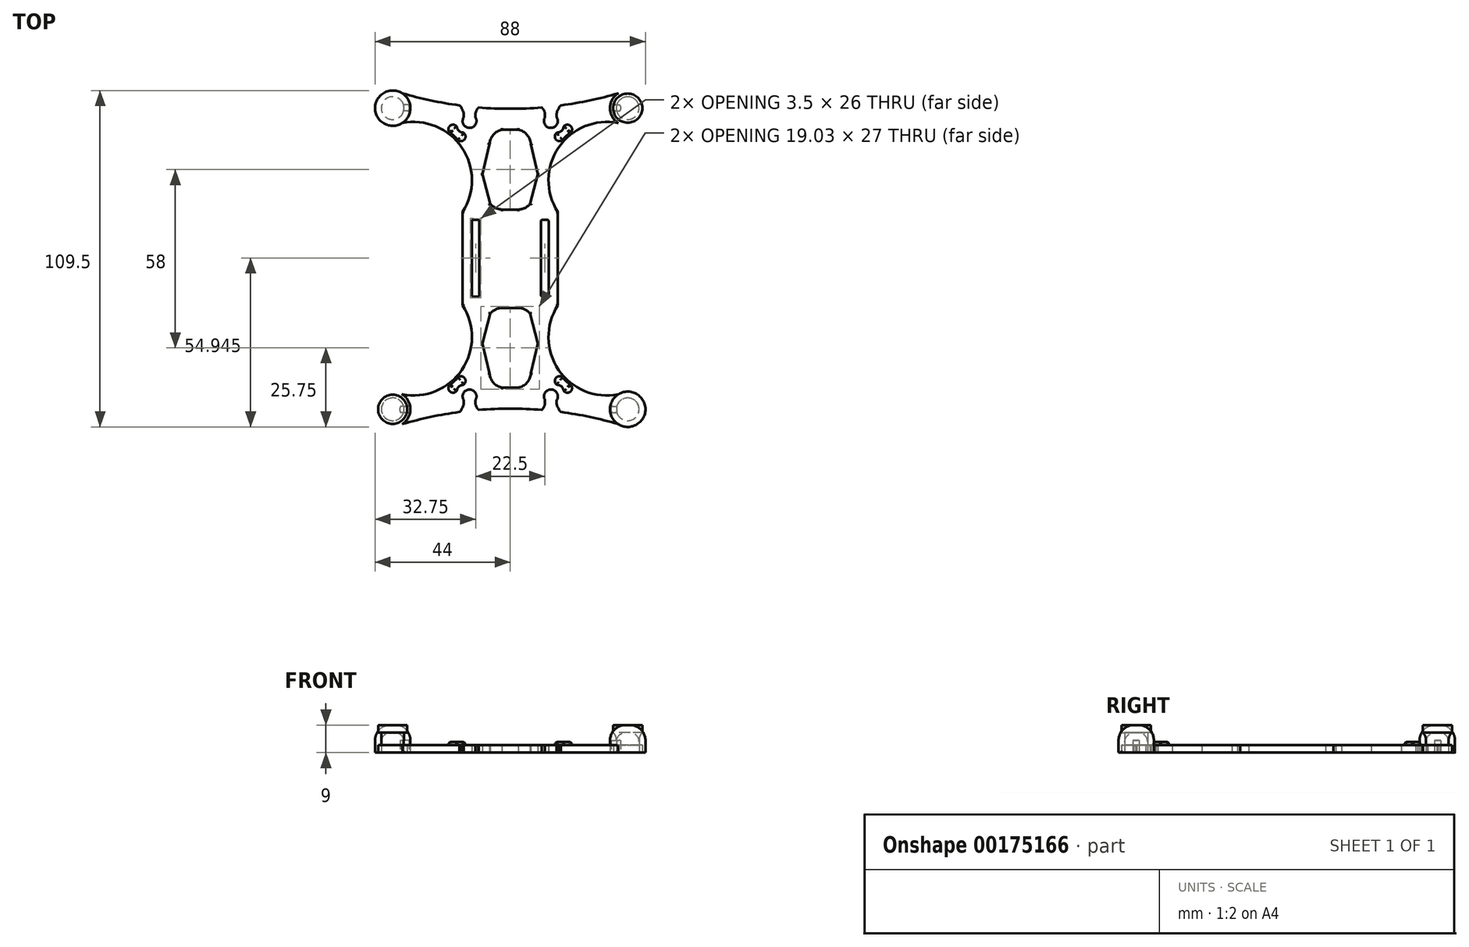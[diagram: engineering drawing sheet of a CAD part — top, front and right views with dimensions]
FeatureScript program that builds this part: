
annotation { "Feature Type Name" : "Feature", "Feature Type Description" : "" }
export const myFeature = defineFeature(function(context is Context, id is Id, definition is map)
    precondition{}
    {
        {
            assignVariable(context, id + "F0", {"name" : "FrameHeight", "anyValue" : 2.5});
        }
        {
            var Q0;
            Q0=qCreatedBy(makeId("Top.planeOp"),FACE);
            var sketch = newSketch(context, id + "F1", { "sketchPlane" : qUnion([Q0])});
            skPoint(sketch, "E0.middle", {"position": v(0, 0) * mm});
            skCircle(sketch, "E1", {"center": v(-38.25, 49) * mm, "radius": 5.75 * mm});
            skCircle(sketch, "E2.MirrorC", {"center": v(38.25, 49) * mm, "radius": 5.75 * mm});
            skCircle(sketch, "E3.MirrorC", {"center": v(-38.25, -49) * mm, "radius": 5.75 * mm});
            skCircle(sketch, "E4.MirrorC", {"center": v(38.25, -49) * mm, "radius": 5.75 * mm});
            skArc(sketch, "E5", {"start": v(-35.12, 53.82) * mm, "mid": v(-25.9, 51.5) * mm, "end": v(-16.55, 49.89) * mm});
            skCircle(sketch, "E6", {"center": v(-38.25, 49) * mm, "radius": 3.7 * mm});
            skCircle(sketch, "E7.MirrorC", {"center": v(38.25, 49) * mm, "radius": 3.7 * mm});
            skCircle(sketch, "E8.MirrorC", {"center": v(38.25, -49) * mm, "radius": 3.7 * mm});
            skCircle(sketch, "E9.MirrorC", {"center": v(-38.25, -49) * mm, "radius": 3.7 * mm});
            skPoint(sketch, "E10.MirrorP", {"position": v(-9, -27.55) * mm});
            skArc(sketch, "E11.MirrorCS", {"start": v(-2.66, -42) * mm, "mid": v(-5.49, -40.33) * mm, "end": v(-6.7, -37.29) * mm});
            skArc(sketch, "E12.MirrorCS", {"start": v(-2.66, -16) * mm, "mid": v(-4.79, -16.51) * mm, "end": v(-6.5, -17.87) * mm});
            skLineSegment(sketch, "E13", {"start": v(-6.5, -17.87) * mm, "end": v(-9, -27.55) * mm});
            skLineSegment(sketch, "E14", {"start": v(-6.7, -37.29) * mm, "end": v(-9, -27.55) * mm});
            skArc(sketch, "E15.MirrorCS", {"start": v(2.66, -16) * mm, "mid": v(4.79, -16.51) * mm, "end": v(6.5, -17.87) * mm});
            skLineSegment(sketch, "E16.MirrorCS", {"start": v(6.5, -17.87) * mm, "end": v(9, -27.55) * mm});
            skLineSegment(sketch, "E17.MirrorCS", {"start": v(6.7, -37.29) * mm, "end": v(9, -27.55) * mm});
            skArc(sketch, "E18.MirrorCS", {"start": v(2.66, -42) * mm, "mid": v(5.49, -40.33) * mm, "end": v(6.7, -37.29) * mm});
            skLineSegment(sketch, "E19", {"start": v(-2.66, -16) * mm, "end": v(2.66, -16) * mm});
            skLineSegment(sketch, "E20", {"start": v(2.66, -42) * mm, "end": v(-2.66, -42) * mm});
            skLineSegment(sketch, "E21.MirrorCS", {"start": v(-2.66, 16) * mm, "end": v(2.66, 16) * mm});
            skArc(sketch, "E22.MirrorCS", {"start": v(-2.66, 16) * mm, "mid": v(-4.79, 16.51) * mm, "end": v(-6.5, 17.87) * mm});
            skLineSegment(sketch, "E23.MirrorCS", {"start": v(-6.5, 17.87) * mm, "end": v(-9, 27.55) * mm});
            skArc(sketch, "E24.MirrorCS", {"start": v(2.66, 16) * mm, "mid": v(4.79, 16.51) * mm, "end": v(6.5, 17.87) * mm});
            skLineSegment(sketch, "E25.MirrorCS", {"start": v(6.5, 17.87) * mm, "end": v(9, 27.55) * mm});
            skLineSegment(sketch, "E26.MirrorCS", {"start": v(-6.7, 37.29) * mm, "end": v(-9, 27.55) * mm});
            skLineSegment(sketch, "E27.MirrorCS", {"start": v(6.7, 37.29) * mm, "end": v(9, 27.55) * mm});
            skArc(sketch, "E28.MirrorCS", {"start": v(2.66, 42) * mm, "mid": v(5.49, 40.33) * mm, "end": v(6.7, 37.29) * mm});
            skLineSegment(sketch, "E29.MirrorCS", {"start": v(2.66, 42) * mm, "end": v(-2.66, 42) * mm});
            skArc(sketch, "E30.MirrorCS", {"start": v(-2.66, 42) * mm, "mid": v(-5.49, 40.33) * mm, "end": v(-6.7, 37.29) * mm});
            skArc(sketch, "E31", {"start": v(-15.5, 15.2) * mm, "mid": v(-15.74, 36.19) * mm, "end": v(-35.17, 44.14) * mm});
            skArc(sketch, "E32.MirrorCS", {"start": v(-35.12, -53.82) * mm, "mid": v(-25.9, -51.5) * mm, "end": v(-16.55, -49.89) * mm});
            skArc(sketch, "E33.MirrorCS", {"start": v(15.5, 15.2) * mm, "mid": v(15.74, 36.19) * mm, "end": v(35.17, 44.14) * mm});
            skArc(sketch, "E34.MirrorCS", {"start": v(15.5, -15.2) * mm, "mid": v(15.74, -36.19) * mm, "end": v(35.17, -44.14) * mm});
            skArc(sketch, "E35.MirrorCS", {"start": v(-15.5, -15.2) * mm, "mid": v(-15.74, -36.19) * mm, "end": v(-35.17, -44.14) * mm});
            skLineSegment(sketch, "E36", {"start": v(-15.5, -15.2) * mm, "end": v(-15.5, 15.2) * mm});
            skLineSegment(sketch, "E37.bottom", {"start": v(-12, -12.3) * mm, "end": v(-10.5, -12.3) * mm});
            skLineSegment(sketch, "E37.top", {"start": v(-12, 12.7) * mm, "end": v(-10.5, 12.7) * mm});
            skLineSegment(sketch, "E37.left", {"start": v(-12.5, -11.8) * mm, "end": v(-12.5, 12.2) * mm});
            skLineSegment(sketch, "E37.right", {"start": v(-10, -11.8) * mm, "end": v(-10, 12.2) * mm});
            skLineSegment(sketch, "E38", {"start": v(-15.5, 15.2) * mm, "end": v(15.5, 15.2) * mm, "construction": true});
            skPoint(sketch, "E39.visualSharp", {"position": v(-10, -12.3) * mm});
            skArc(sketch, "E39.filletArc", {"start": v(-10.5, -12.3) * mm, "mid": v(-10.15, -12.16) * mm, "end": v(-10, -11.8) * mm});
            skPoint(sketch, "E40.visualSharp", {"position": v(-12.5, -12.3) * mm});
            skArc(sketch, "E40.filletArc", {"start": v(-12.5, -11.8) * mm, "mid": v(-12.35, -12.16) * mm, "end": v(-12, -12.3) * mm});
            skPoint(sketch, "E41.visualSharp", {"position": v(-10, 12.7) * mm});
            skArc(sketch, "E41.filletArc", {"start": v(-10, 12.2) * mm, "mid": v(-10.15, 12.55) * mm, "end": v(-10.5, 12.7) * mm});
            skPoint(sketch, "E42.visualSharp", {"position": v(-12.5, 12.7) * mm});
            skArc(sketch, "E42.filletArc", {"start": v(-12, 12.7) * mm, "mid": v(-12.35, 12.55) * mm, "end": v(-12.5, 12.2) * mm});
            skLineSegment(sketch, "E43.MirrorCS", {"start": v(12, -12.3) * mm, "end": v(10.5, -12.3) * mm});
            skArc(sketch, "E44.MirrorCS", {"start": v(12.5, -11.8) * mm, "mid": v(12.35, -12.16) * mm, "end": v(12, -12.3) * mm});
            skArc(sketch, "E45.MirrorCS", {"start": v(10.5, -12.3) * mm, "mid": v(10.15, -12.16) * mm, "end": v(10, -11.8) * mm});
            skLineSegment(sketch, "E46.MirrorCS", {"start": v(10, -11.8) * mm, "end": v(10, 12.2) * mm});
            skLineSegment(sketch, "E47.MirrorCS", {"start": v(12.5, -11.8) * mm, "end": v(12.5, 12.2) * mm});
            skArc(sketch, "E48.MirrorCS", {"start": v(10, 12.2) * mm, "mid": v(10.15, 12.55) * mm, "end": v(10.5, 12.7) * mm});
            skLineSegment(sketch, "E49.MirrorCS", {"start": v(12, 12.7) * mm, "end": v(10.5, 12.7) * mm});
            skArc(sketch, "E50.MirrorCS", {"start": v(12, 12.7) * mm, "mid": v(12.35, 12.55) * mm, "end": v(12.5, 12.2) * mm});
            skLineSegment(sketch, "E51", {"start": v(15.5, 15.2) * mm, "end": v(15.5, -15.2) * mm});
            skArc(sketch, "E52.trimOffspring", {"start": v(-10.28, 49.21) * mm, "mid": v(0, 48.79) * mm, "end": v(10.28, 49.21) * mm});
            skArc(sketch, "E53", {"start": v(-15.18, 45.95) * mm, "mid": v(-13.3, 42.57) * mm, "end": v(-11.24, 45.85) * mm});
            skArc(sketch, "E54", {"start": v(-15.18, 45.95) * mm, "mid": v(-15.18, 47.49) * mm, "end": v(-15.83, 48.88) * mm});
            skArc(sketch, "E55.MirrorCS", {"start": v(-11.24, 45.85) * mm, "mid": v(-11.2, 47.66) * mm, "end": v(-10.28, 49.21) * mm});
            skArc(sketch, "E56.trimOffspring", {"start": v(16.55, 49.89) * mm, "mid": v(25.9, 51.5) * mm, "end": v(35.12, 53.82) * mm});
            skArc(sketch, "E57.trimOffspring", {"start": v(-10.28, -49.21) * mm, "mid": v(0, -48.79) * mm, "end": v(10.28, -49.21) * mm});
            skArc(sketch, "E58.trimOffspring", {"start": v(16.55, -49.89) * mm, "mid": v(25.9, -51.5) * mm, "end": v(35.12, -53.82) * mm});
            skArc(sketch, "E59.MirrorCS", {"start": v(11.24, 45.85) * mm, "mid": v(11.2, 47.66) * mm, "end": v(10.28, 49.21) * mm});
            skArc(sketch, "E60.MirrorCS", {"start": v(15.18, 45.95) * mm, "mid": v(15.18, 47.49) * mm, "end": v(15.83, 48.88) * mm});
            skArc(sketch, "E61.MirrorCS", {"start": v(15.18, 45.95) * mm, "mid": v(13.3, 42.57) * mm, "end": v(11.24, 45.85) * mm});
            skArc(sketch, "E62.MirrorCS", {"start": v(15.18, -45.95) * mm, "mid": v(13.3, -42.57) * mm, "end": v(11.24, -45.85) * mm});
            skArc(sketch, "E63.MirrorCS", {"start": v(11.24, -45.85) * mm, "mid": v(11.2, -47.66) * mm, "end": v(10.28, -49.21) * mm});
            skArc(sketch, "E64.MirrorCS", {"start": v(15.18, -45.95) * mm, "mid": v(15.18, -47.49) * mm, "end": v(15.83, -48.88) * mm});
            skArc(sketch, "E65.MirrorCS", {"start": v(-11.24, -45.85) * mm, "mid": v(-11.2, -47.66) * mm, "end": v(-10.28, -49.21) * mm});
            skArc(sketch, "E66.MirrorCS", {"start": v(-15.18, -45.95) * mm, "mid": v(-15.18, -47.49) * mm, "end": v(-15.83, -48.88) * mm});
            skArc(sketch, "E67.MirrorCS", {"start": v(-15.18, -45.95) * mm, "mid": v(-13.3, -42.57) * mm, "end": v(-11.24, -45.85) * mm});
            skLineSegment(sketch, "E68", {"start": v(-38.25, 49) * mm, "end": v(38.25, 49) * mm, "construction": true});
            skArc(sketch, "E69", {"start": v(16.55, 49.89) * mm, "mid": v(16.05, 49.49) * mm, "end": v(15.83, 48.88) * mm});
            skArc(sketch, "E70.MirrorCS", {"start": v(-16.55, 49.89) * mm, "mid": v(-16.05, 49.49) * mm, "end": v(-15.83, 48.88) * mm});
            skArc(sketch, "E71.MirrorCS", {"start": v(-16.55, -49.89) * mm, "mid": v(-16.05, -49.49) * mm, "end": v(-15.83, -48.88) * mm});
            skArc(sketch, "E72.MirrorCS", {"start": v(16.55, -49.89) * mm, "mid": v(16.05, -49.49) * mm, "end": v(15.83, -48.88) * mm});
            skLineSegment(sketch, "E73", {"start": v(-38.25, -49) * mm, "end": v(38.25, 49) * mm, "construction": true});
            skCircle(sketch, "E74", {"center": v(-38.25, 49) * mm, "radius": 4.75 * mm});
            skCircle(sketch, "E75.MirrorC", {"center": v(38.25, 49) * mm, "radius": 4.75 * mm});
            skCircle(sketch, "E76.MirrorC", {"center": v(38.25, -49) * mm, "radius": 4.75 * mm});
            skCircle(sketch, "E77.MirrorC", {"center": v(-38.25, -49) * mm, "radius": 4.75 * mm});
            skSolve(sketch);
        }
        {
            var Q0;
            {var subQ4=sQuery(id+"F1.wireOp",EDGE,"E5");Q0=makeQuery(id+"F1.imprint","IMPRINT",FACE,{"disambiguationData":[TD([[makeQuery(id+"F1.imprint","IMPRINT",EDGE,{"derivedFrom":subQ4}),-1.0]])]});}
            var Q1;
            Q1=makeQuery(id+"F1.imprint","IMPRINT",FACE,{"disambiguationData":[TD([[makeQuery(id+"F1.imprint","IMPRINT",EDGE,{"derivedFrom":sQuery(id+"F1.wireOp",EDGE,"E9.MirrorC")}),1.0]])]});
            var Q2;
            Q2=makeQuery(id+"F1.imprint","IMPRINT",FACE,{"disambiguationData":[TD([[makeQuery(id+"F1.imprint","IMPRINT",EDGE,{"derivedFrom":sQuery(id+"F1.wireOp",EDGE,"E8.MirrorC")}),-1.0]])]});
            var Q3;
            Q3=makeQuery(id+"F1.imprint","IMPRINT",FACE,{"disambiguationData":[TD([[makeQuery(id+"F1.imprint","IMPRINT",EDGE,{"derivedFrom":sQuery(id+"F1.wireOp",EDGE,"E6")}),-1.0]])]});
            var Q4;
            Q4=makeQuery(id+"F1.imprint","IMPRINT",FACE,{"disambiguationData":[TD([[makeQuery(id+"F1.imprint","IMPRINT",EDGE,{"derivedFrom":sQuery(id+"F1.wireOp",EDGE,"E7.MirrorC")}),1.0]])]});
            var Q5;
            {var subQ0=sQuery(id+"F1.wireOp",EDGE,"7a08c846-7200-404a-ab22-a396ae0e95b40.MirrorCS");Q5=makeQuery(id+"F1.imprint","IMPRINT",FACE,{"disambiguationData":[TD([[makeQuery(id+"F1.imprint","IMPRINT",EDGE,{"derivedFrom":subQ0}),-1.0]])]});}
            extrude(context, id + "F2", {"entities" : qUnion([Q0, Q1, Q2, Q3, Q4, Q5]), "depth" : 2.5 * mm});
        }
        {
            var Q0;
            Q0=makeQuery(id+"F1.imprint","IMPRINT",FACE,{"disambiguationData":[TD([[makeQuery(id+"F1.imprint","IMPRINT",EDGE,{"derivedFrom":sQuery(id+"F1.wireOp",EDGE,"E74")}),-1.0]])]});
            var Q1;
            Q1=makeQuery(id+"F1.imprint","IMPRINT",FACE,{"disambiguationData":[TD([[makeQuery(id+"F1.imprint","IMPRINT",EDGE,{"derivedFrom":sQuery(id+"F1.wireOp",EDGE,"E75.MirrorC")}),1.0]])]});
            var Q2;
            Q2=makeQuery(id+"F1.imprint","IMPRINT",FACE,{"disambiguationData":[TD([[makeQuery(id+"F1.imprint","IMPRINT",EDGE,{"derivedFrom":sQuery(id+"F1.wireOp",EDGE,"E77.MirrorC")}),1.0]])]});
            var Q3;
            Q3=makeQuery(id+"F1.imprint","IMPRINT",FACE,{"disambiguationData":[TD([[makeQuery(id+"F1.imprint","IMPRINT",EDGE,{"derivedFrom":sQuery(id+"F1.wireOp",EDGE,"E76.MirrorC")}),-1.0]])]});
            extrude(context, id + "F3", {"entities" : qUnion([Q0, Q1, Q2, Q3]), "operationType" : NewBodyOperationType.ADD, "depth" : 3 * mm});
        }
        {
            var Q0;
            Q0=makeQuery(id+"F1.imprint","IMPRINT",FACE,{"disambiguationData":[TD([[makeQuery(id+"F1.imprint","IMPRINT",EDGE,{"derivedFrom":sQuery(id+"F1.wireOp",EDGE,"E6")}),-1.0]])]});
            var Q1;
            Q1=makeQuery(id+"F1.imprint","IMPRINT",FACE,{"disambiguationData":[TD([[makeQuery(id+"F1.imprint","IMPRINT",EDGE,{"derivedFrom":sQuery(id+"F1.wireOp",EDGE,"E7.MirrorC")}),1.0]])]});
            var Q2;
            Q2=makeQuery(id+"F1.imprint","IMPRINT",FACE,{"disambiguationData":[TD([[makeQuery(id+"F1.imprint","IMPRINT",EDGE,{"derivedFrom":sQuery(id+"F1.wireOp",EDGE,"E9.MirrorC")}),1.0]])]});
            var Q3;
            Q3=makeQuery(id+"F1.imprint","IMPRINT",FACE,{"disambiguationData":[TD([[makeQuery(id+"F1.imprint","IMPRINT",EDGE,{"derivedFrom":sQuery(id+"F1.wireOp",EDGE,"E8.MirrorC")}),-1.0]])]});
            var Q4;
            Q4=makeQuery(id+"F1.imprint","IMPRINT",FACE,{"disambiguationData":[TD([[makeQuery(id+"F1.imprint","IMPRINT",EDGE,{"derivedFrom":sQuery(id+"F1.wireOp",EDGE,"E6")}),1.0]])]});
            var Q5;
            Q5=makeQuery(id+"F1.imprint","IMPRINT",FACE,{"disambiguationData":[TD([[makeQuery(id+"F1.imprint","IMPRINT",EDGE,{"derivedFrom":sQuery(id+"F1.wireOp",EDGE,"E7.MirrorC")}),-1.0]])]});
            var Q6;
            Q6=makeQuery(id+"F1.imprint","IMPRINT",FACE,{"disambiguationData":[TD([[makeQuery(id+"F1.imprint","IMPRINT",EDGE,{"derivedFrom":sQuery(id+"F1.wireOp",EDGE,"E8.MirrorC")}),1.0]])]});
            var Q7;
            Q7=makeQuery(id+"F1.imprint","IMPRINT",FACE,{"disambiguationData":[TD([[makeQuery(id+"F1.imprint","IMPRINT",EDGE,{"derivedFrom":sQuery(id+"F1.wireOp",EDGE,"E9.MirrorC")}),-1.0]])]});
            var Q8;
            {var subQ0=sQuery(id+"F1.wireOp",EDGE,"ea4f1012-2509-42ab-b6be-2330c5534f0a0.MirrorCS");var subQ1=sQuery(id+"F1.wireOp",EDGE,"cdfdab9b-bf2e-43ec-8392-f97786d2ea0d0.MirrorCS");var subQ2=sQuery(id+"F1.wireOp",EDGE,"465e94d3-5aed-43b1-ab28-4905a897ac150.MirrorCS");var subQ3=sQuery(id+"F1.wireOp",EDGE,"98a759bb-2186-4722-986c-5ad8236f98b60.MirrorCS");var subQ4=sQuery(id+"F1.wireOp",EDGE,"529e4913-d2e2-4b9c-8764-fd74a515156b0.MirrorCS");var subQ5=sQuery(id+"F1.wireOp",EDGE,"a75351e4-8b9f-4b28-a4a3-4962784478ad0.MirrorCS");var subQ6=sQuery(id+"F1.wireOp",EDGE,"82538637-7302-4e28-b2d0-c30d791653240.MirrorCS");var subQ7=sQuery(id+"F1.wireOp",EDGE,"56e68159-8ace-49cd-9e0b-4dd6a05a3e180.MirrorCS");var subQ8=sQuery(id+"F1.wireOp",EDGE,"e7e79bb3-8a2c-4938-af19-8f637f7eba370.MirrorCS");var subQ9=sQuery(id+"F1.wireOp",EDGE,"2316bcf3-3be9-4e9e-b8e2-497a6a1952b90.MirrorCS");var subQ10=sQuery(id+"F1.wireOp",EDGE,"1773aba8-4819-4f46-a8a7-8d94881a3e2a0.MirrorCS");var subQ11=sQuery(id+"F1.wireOp",EDGE,"e0e34dce-b0e1-4d64-a790-8c4829cf73b10.MirrorCS");var subQ12=sQuery(id+"F1.wireOp",EDGE,"8cd6d0e1-198d-4ddf-9674-687771b3d4800.MirrorCS");var subQ13=sQuery(id+"F1.wireOp",EDGE,"258af2fb-57e0-4cd8-8c30-8cafca4a9de30.MirrorCS");var subQ14=sQuery(id+"F1.wireOp",EDGE,"a07b8381-fd63-4e58-856e-6aaff1297d55.filletArc");var subQ15=sQuery(id+"F1.wireOp",EDGE,"RvagwD08-4saL-jRzY-J36Z-niyVwtinKrBz");var subQ16=sQuery(id+"F1.wireOp",EDGE,"o4VfrY1E-f77m-jJ6D-3hSz-oWbsnZmPJ7RM");var subQ17=sQuery(id+"F1.wireOp",EDGE,"5SzH9PIc-MBC3-JWxo-jWJ1-gy0vg8dHxIne");var subQ18=sQuery(id+"F1.wireOp",EDGE,"Skl9KyDn-OFwj-jcuM-sPno-qYqNKXC7fZA3");var subQ19=sQuery(id+"F1.wireOp",EDGE,"5RGUndvU-jcMW-WSWi-Bxv8-2VV6o0UGLXlU");var subQ20=sQuery(id+"F1.wireOp",EDGE,"NKQneA6F-sO9O-ycv6-QC4M-7Sw9j2aKeUUz");var subQ21=sQuery(id+"F1.wireOp",EDGE,"41db651c-dc80-447a-ac2a-c1855a6981c0.filletArc");var subQ22=sQuery(id+"F1.wireOp",EDGE,"cd34b8fd-3b9d-40b5-866b-1931df3bf95f.filletArc");var subQ23=sQuery(id+"F1.wireOp",EDGE,"e2ad8a51-9023-4a85-890f-8adf256902f4.filletArc");var subQ24=sQuery(id+"F1.wireOp",EDGE,"f659aba6-3ceb-4f67-afd8-6bc25f8b2d52.filletArc");var subQ25=sQuery(id+"F1.wireOp",EDGE,"E30.MirrorCS");var subQ26=sQuery(id+"F1.wireOp",EDGE,"E29.MirrorCS");var subQ27=sQuery(id+"F1.wireOp",EDGE,"E28.MirrorCS");var subQ28=sQuery(id+"F1.wireOp",EDGE,"E27.MirrorCS");var subQ29=sQuery(id+"F1.wireOp",EDGE,"E26.MirrorCS");var subQ30=sQuery(id+"F1.wireOp",EDGE,"E25.MirrorCS");var subQ31=sQuery(id+"F1.wireOp",EDGE,"E24.MirrorCS");var subQ32=sQuery(id+"F1.wireOp",EDGE,"E23.MirrorCS");var subQ33=sQuery(id+"F1.wireOp",EDGE,"E22.MirrorCS");var subQ34=sQuery(id+"F1.wireOp",EDGE,"E21.MirrorCS");var subQ35=sQuery(id+"F1.wireOp",EDGE,"E20");var subQ36=sQuery(id+"F1.wireOp",EDGE,"E19");var subQ37=sQuery(id+"F1.wireOp",EDGE,"E18.MirrorCS");var subQ38=sQuery(id+"F1.wireOp",EDGE,"E17.MirrorCS");var subQ39=sQuery(id+"F1.wireOp",EDGE,"E16.MirrorCS");var subQ40=sQuery(id+"F1.wireOp",EDGE,"E15.MirrorCS");var subQ41=sQuery(id+"F1.wireOp",EDGE,"E14");var subQ42=sQuery(id+"F1.wireOp",EDGE,"E13");var subQ43=sQuery(id+"F1.wireOp",EDGE,"E12.MirrorCS");var subQ44=sQuery(id+"F1.wireOp",EDGE,"E11.MirrorCS");var subQ45=sQuery(id+"F1.wireOp",EDGE,"8O0KtBdD-sCAZ-nUyN-ZE4b-Pr8atPqkOLOt.right");var subQ46=sQuery(id+"F1.wireOp",EDGE,"8O0KtBdD-sCAZ-nUyN-ZE4b-Pr8atPqkOLOt.top");var subQ47=sQuery(id+"F1.wireOp",EDGE,"8O0KtBdD-sCAZ-nUyN-ZE4b-Pr8atPqkOLOt.bottom");var subQ48=sQuery(id+"F1.wireOp",EDGE,"3a3e3443-e76c-4b3f-931a-bba0a9ca54bb0.MirrorC");var subQ49=sQuery(id+"F1.wireOp",EDGE,"5ae8c34d-aa19-45d0-b816-4b0481c35e6e0.MirrorC");var subQ50=sQuery(id+"F1.wireOp",EDGE,"e54bd452-817c-44b1-b4a1-4a82a5b737490.MirrorC");var subQ51=sQuery(id+"F1.wireOp",EDGE,"vB4YpJxw-nM1r-KAMU-Z2z7-AA1Xbjjr12VQ");var subQ52=sQuery(id+"F1.wireOp",EDGE,"2126723b-73e3-4daa-88ad-461916ae88fc0.MirrorCS");var subQ53=sQuery(id+"F1.wireOp",EDGE,"8d91ff8a-54ff-47bb-bb8d-6ed09a5a66a50.MirrorCS");var subQ54=sQuery(id+"F1.wireOp",EDGE,"462311f5-9079-46a5-b6e4-7ace82524d020.MirrorCS");var subQ55=sQuery(id+"F1.wireOp",EDGE,"8mwgoKQL-uejJ-Ytzu-yeJP-nfI78MkwDY2L");var subQ56=sQuery(id+"F1.wireOp",EDGE,"3589fe97-52ff-42bc-b7a9-5f631560aecf0.MirrorCS");var subQ57=sQuery(id+"F1.wireOp",EDGE,"E5");var subQ58=sQuery(id+"F1.wireOp",EDGE,"E4.MirrorC");var subQ59=sQuery(id+"F1.wireOp",EDGE,"E3.MirrorC");var subQ60=sQuery(id+"F1.wireOp",EDGE,"E2.MirrorC");var subQ61=sQuery(id+"F1.wireOp",EDGE,"E1");Q8=makeQuery(id+"FTKf5rjYO4gTYV3_1.boolean.opBoolean","MERGE",FACE,{"derivedFrom":[makeQuery(id+"FOrR15PyCScxact_0.opExtrude","CAP_FACE",FACE,{"disambiguationData":[OSD([subQ61,subQ60,subQ59,subQ58,subQ57,subQ56,subQ55,subQ54,subQ53,subQ52,subQ51,subQ50,subQ49,subQ48,subQ47,subQ46,subQ45,subQ44,subQ43,subQ42,subQ41,subQ40,subQ39,subQ38,subQ37,subQ36,subQ35,subQ34,subQ33,subQ32,subQ31,subQ30,subQ29,subQ28,subQ27,subQ26,subQ25,subQ24,subQ23,subQ22,subQ21,subQ20,subQ19,subQ18,subQ17,subQ16,subQ15,subQ14,subQ13,subQ12,subQ11,subQ10,subQ9,subQ8,subQ7,subQ6,subQ5,subQ4,subQ3,subQ2,subQ1,subQ0])],"isStart":false}),makeQuery(id+"FTKf5rjYO4gTYV3_1.opExtrude","CAP_FACE",FACE,{"disambiguationData":[OSD([subQ61,subQ60,subQ59,subQ58,subQ57,subQ56,sQuery(id+"F1.wireOp",EDGE,"E6"),subQ55,subQ54,subQ53,subQ52,sQuery(id+"F1.wireOp",EDGE,"E7.MirrorC"),sQuery(id+"F1.wireOp",EDGE,"E8.MirrorC"),sQuery(id+"F1.wireOp",EDGE,"E9.MirrorC"),subQ51,subQ50,subQ49,subQ48,subQ47,subQ46,subQ45,subQ44,subQ43,subQ42,subQ41,subQ40,subQ39,subQ38,subQ37,subQ36,subQ35,subQ34,subQ33,subQ32,subQ31,subQ30,subQ29,subQ28,subQ27,subQ26,subQ25,subQ24,subQ23,subQ22,subQ21,subQ20,subQ19,subQ18,subQ17,subQ16,subQ15,subQ14,subQ13,subQ12,subQ11,subQ10,subQ9,subQ8,subQ7,subQ6,subQ5,subQ4,subQ3,subQ2,subQ1,subQ0])],"isStart":false})]});}
            var Q9;
            Q9=makeQuery(id+"FOrR15PyCScxact_0.opExtrude","SWEPT_BODY",BODY,{"disambiguationData":[OSD([sQuery(id+"F1.wireOp",EDGE,"E1"),sQuery(id+"F1.wireOp",EDGE,"E2.MirrorC"),sQuery(id+"F1.wireOp",EDGE,"E3.MirrorC"),sQuery(id+"F1.wireOp",EDGE,"E4.MirrorC"),sQuery(id+"F1.wireOp",EDGE,"E5"),sQuery(id+"F1.wireOp",EDGE,"3589fe97-52ff-42bc-b7a9-5f631560aecf0.MirrorCS"),sQuery(id+"F1.wireOp",EDGE,"8mwgoKQL-uejJ-Ytzu-yeJP-nfI78MkwDY2L"),sQuery(id+"F1.wireOp",EDGE,"462311f5-9079-46a5-b6e4-7ace82524d020.MirrorCS"),sQuery(id+"F1.wireOp",EDGE,"8d91ff8a-54ff-47bb-bb8d-6ed09a5a66a50.MirrorCS"),sQuery(id+"F1.wireOp",EDGE,"2126723b-73e3-4daa-88ad-461916ae88fc0.MirrorCS"),sQuery(id+"F1.wireOp",EDGE,"vB4YpJxw-nM1r-KAMU-Z2z7-AA1Xbjjr12VQ"),sQuery(id+"F1.wireOp",EDGE,"e54bd452-817c-44b1-b4a1-4a82a5b737490.MirrorC"),sQuery(id+"F1.wireOp",EDGE,"5ae8c34d-aa19-45d0-b816-4b0481c35e6e0.MirrorC"),sQuery(id+"F1.wireOp",EDGE,"3a3e3443-e76c-4b3f-931a-bba0a9ca54bb0.MirrorC"),sQuery(id+"F1.wireOp",EDGE,"8O0KtBdD-sCAZ-nUyN-ZE4b-Pr8atPqkOLOt.bottom"),sQuery(id+"F1.wireOp",EDGE,"8O0KtBdD-sCAZ-nUyN-ZE4b-Pr8atPqkOLOt.top"),sQuery(id+"F1.wireOp",EDGE,"8O0KtBdD-sCAZ-nUyN-ZE4b-Pr8atPqkOLOt.right"),sQuery(id+"F1.wireOp",EDGE,"E11.MirrorCS"),sQuery(id+"F1.wireOp",EDGE,"E12.MirrorCS"),sQuery(id+"F1.wireOp",EDGE,"E13"),sQuery(id+"F1.wireOp",EDGE,"E14"),sQuery(id+"F1.wireOp",EDGE,"E15.MirrorCS"),sQuery(id+"F1.wireOp",EDGE,"E16.MirrorCS"),sQuery(id+"F1.wireOp",EDGE,"E17.MirrorCS"),sQuery(id+"F1.wireOp",EDGE,"E18.MirrorCS"),sQuery(id+"F1.wireOp",EDGE,"E19"),sQuery(id+"F1.wireOp",EDGE,"E20"),sQuery(id+"F1.wireOp",EDGE,"E21.MirrorCS"),sQuery(id+"F1.wireOp",EDGE,"E22.MirrorCS"),sQuery(id+"F1.wireOp",EDGE,"E23.MirrorCS"),sQuery(id+"F1.wireOp",EDGE,"E24.MirrorCS"),sQuery(id+"F1.wireOp",EDGE,"E25.MirrorCS"),sQuery(id+"F1.wireOp",EDGE,"E26.MirrorCS"),sQuery(id+"F1.wireOp",EDGE,"E27.MirrorCS"),sQuery(id+"F1.wireOp",EDGE,"E28.MirrorCS"),sQuery(id+"F1.wireOp",EDGE,"E29.MirrorCS"),sQuery(id+"F1.wireOp",EDGE,"E30.MirrorCS"),sQuery(id+"F1.wireOp",EDGE,"f659aba6-3ceb-4f67-afd8-6bc25f8b2d52.filletArc"),sQuery(id+"F1.wireOp",EDGE,"e2ad8a51-9023-4a85-890f-8adf256902f4.filletArc"),sQuery(id+"F1.wireOp",EDGE,"cd34b8fd-3b9d-40b5-866b-1931df3bf95f.filletArc"),sQuery(id+"F1.wireOp",EDGE,"41db651c-dc80-447a-ac2a-c1855a6981c0.filletArc"),sQuery(id+"F1.wireOp",EDGE,"NKQneA6F-sO9O-ycv6-QC4M-7Sw9j2aKeUUz"),sQuery(id+"F1.wireOp",EDGE,"5RGUndvU-jcMW-WSWi-Bxv8-2VV6o0UGLXlU"),sQuery(id+"F1.wireOp",EDGE,"Skl9KyDn-OFwj-jcuM-sPno-qYqNKXC7fZA3"),sQuery(id+"F1.wireOp",EDGE,"5SzH9PIc-MBC3-JWxo-jWJ1-gy0vg8dHxIne"),sQuery(id+"F1.wireOp",EDGE,"o4VfrY1E-f77m-jJ6D-3hSz-oWbsnZmPJ7RM"),sQuery(id+"F1.wireOp",EDGE,"RvagwD08-4saL-jRzY-J36Z-niyVwtinKrBz"),sQuery(id+"F1.wireOp",EDGE,"a07b8381-fd63-4e58-856e-6aaff1297d55.filletArc"),sQuery(id+"F1.wireOp",EDGE,"258af2fb-57e0-4cd8-8c30-8cafca4a9de30.MirrorCS"),sQuery(id+"F1.wireOp",EDGE,"8cd6d0e1-198d-4ddf-9674-687771b3d4800.MirrorCS"),sQuery(id+"F1.wireOp",EDGE,"e0e34dce-b0e1-4d64-a790-8c4829cf73b10.MirrorCS"),sQuery(id+"F1.wireOp",EDGE,"1773aba8-4819-4f46-a8a7-8d94881a3e2a0.MirrorCS"),sQuery(id+"F1.wireOp",EDGE,"2316bcf3-3be9-4e9e-b8e2-497a6a1952b90.MirrorCS"),sQuery(id+"F1.wireOp",EDGE,"e7e79bb3-8a2c-4938-af19-8f637f7eba370.MirrorCS"),sQuery(id+"F1.wireOp",EDGE,"56e68159-8ace-49cd-9e0b-4dd6a05a3e180.MirrorCS"),sQuery(id+"F1.wireOp",EDGE,"82538637-7302-4e28-b2d0-c30d791653240.MirrorCS"),sQuery(id+"F1.wireOp",EDGE,"a75351e4-8b9f-4b28-a4a3-4962784478ad0.MirrorCS"),sQuery(id+"F1.wireOp",EDGE,"529e4913-d2e2-4b9c-8764-fd74a515156b0.MirrorCS"),sQuery(id+"F1.wireOp",EDGE,"98a759bb-2186-4722-986c-5ad8236f98b60.MirrorCS"),sQuery(id+"F1.wireOp",EDGE,"465e94d3-5aed-43b1-ab28-4905a897ac150.MirrorCS"),sQuery(id+"F1.wireOp",EDGE,"cdfdab9b-bf2e-43ec-8392-f97786d2ea0d0.MirrorCS"),sQuery(id+"F1.wireOp",EDGE,"ea4f1012-2509-42ab-b6be-2330c5534f0a0.MirrorCS")])]});
            extrude(context, id + "F4", {"entities" : qUnion([Q0, Q1, Q2, Q3, Q4, Q5, Q6, Q7]), "depth" : 9 * mm, "hasSecondDirection" : true, "secondDirectionOppositeDirection" : false, "secondDirectionBoundEntityFace" : qUnion([Q8]), "secondDirectionBoundEntityBody" : qUnion([Q9]), "secondDirectionDepth" : (getVariable(context, 'FrameHeight')) * mm});
        }
        {
            var Q0;
            Q0=makeQuery(id+"F1.imprint","IMPRINT",FACE,{"disambiguationData":[TD([[makeQuery(id+"F1.imprint","IMPRINT",EDGE,{"derivedFrom":sQuery(id+"F1.wireOp",EDGE,"E77.MirrorC")}),1.0]])]});
            var Q1;
            Q1=makeQuery(id+"F1.imprint","IMPRINT",FACE,{"disambiguationData":[TD([[makeQuery(id+"F1.imprint","IMPRINT",EDGE,{"derivedFrom":sQuery(id+"F1.wireOp",EDGE,"E74")}),-1.0]])]});
            var Q2;
            Q2=makeQuery(id+"F1.imprint","IMPRINT",FACE,{"disambiguationData":[TD([[makeQuery(id+"F1.imprint","IMPRINT",EDGE,{"derivedFrom":sQuery(id+"F1.wireOp",EDGE,"E76.MirrorC")}),-1.0]])]});
            var Q3;
            Q3=makeQuery(id+"F1.imprint","IMPRINT",FACE,{"disambiguationData":[TD([[makeQuery(id+"F1.imprint","IMPRINT",EDGE,{"derivedFrom":sQuery(id+"F1.wireOp",EDGE,"E75.MirrorC")}),1.0]])]});
            extrude(context, id + "F5", {"entities" : qUnion([Q0, Q1, Q2, Q3]), "operationType" : NewBodyOperationType.ADD, "depth" : 9 * mm, "hasSecondDirection" : true, "secondDirectionOppositeDirection" : false, "secondDirectionDepth" : 3 * mm});
        }
        {
            var Q0;
            Q0=makeQuery(id+"F1.imprint","IMPRINT",FACE,{"disambiguationData":[TD([[makeQuery(id+"F1.imprint","IMPRINT",EDGE,{"derivedFrom":sQuery(id+"F1.wireOp",EDGE,"E6")}),1.0]])]});
            var Q1;
            Q1=makeQuery(id+"F1.imprint","IMPRINT",FACE,{"disambiguationData":[TD([[makeQuery(id+"F1.imprint","IMPRINT",EDGE,{"derivedFrom":sQuery(id+"F1.wireOp",EDGE,"E7.MirrorC")}),-1.0]])]});
            var Q2;
            Q2=makeQuery(id+"F1.imprint","IMPRINT",FACE,{"disambiguationData":[TD([[makeQuery(id+"F1.imprint","IMPRINT",EDGE,{"derivedFrom":sQuery(id+"F1.wireOp",EDGE,"E9.MirrorC")}),-1.0]])]});
            var Q3;
            Q3=makeQuery(id+"F1.imprint","IMPRINT",FACE,{"disambiguationData":[TD([[makeQuery(id+"F1.imprint","IMPRINT",EDGE,{"derivedFrom":sQuery(id+"F1.wireOp",EDGE,"E8.MirrorC")}),1.0]])]});
            extrude(context, id + "F6", {"entities" : qUnion([Q0, Q1, Q2, Q3]), "operationType" : NewBodyOperationType.REMOVE, "depth" : 6.5 * mm, "hasSecondDirection" : true, "secondDirectionOppositeDirection" : false, "secondDirectionDepth" : 2.5 * mm});
        }
        {
            var Q0;
            Q0=makeQuery(id+"F5.opExtrude","CAP_EDGE",EDGE,{"disambiguationData":[OSD([sQuery(id+"F1.wireOp",EDGE,"E1")])],"isStart":false});
            var Q1;
            Q1=makeQuery(id+"F5.opExtrude","CAP_EDGE",EDGE,{"disambiguationData":[OSD([sQuery(id+"F1.wireOp",EDGE,"E2.MirrorC")])],"isStart":false});
            var Q2;
            Q2=makeQuery(id+"F5.opExtrude","CAP_EDGE",EDGE,{"disambiguationData":[OSD([sQuery(id+"F1.wireOp",EDGE,"E4.MirrorC")])],"isStart":false});
            var Q3;
            Q3=makeQuery(id+"F5.opExtrude","CAP_EDGE",EDGE,{"disambiguationData":[OSD([sQuery(id+"F1.wireOp",EDGE,"E3.MirrorC")])],"isStart":false});
            fillet(context, id + "F7", {"entities" : qUnion([Q0, Q1, Q2, Q3]), "radius" : 5 * mm, "tangentPropagation" : true, "allowEdgeOverflow" : false});
        }
        {
            var Q0;
            Q0=makeQuery(id+"F6.boolean.opBoolean","COPY",EDGE,{"derivedFrom":makeQuery(id+"F6.opExtrude","CAP_EDGE",EDGE,{"disambiguationData":[OSD([sQuery(id+"F1.wireOp",EDGE,"E6")])],"isStart":false})});
            var Q1;
            Q1=makeQuery(id+"F6.boolean.opBoolean","COPY",EDGE,{"derivedFrom":makeQuery(id+"F6.opExtrude","CAP_EDGE",EDGE,{"disambiguationData":[OSD([sQuery(id+"F1.wireOp",EDGE,"E7.MirrorC")])],"isStart":false})});
            var Q2;
            Q2=makeQuery(id+"F6.boolean.opBoolean","COPY",FACE,{"derivedFrom":makeQuery(id+"F6.opExtrude","CAP_FACE",FACE,{"disambiguationData":[OSD([sQuery(id+"F1.wireOp",EDGE,"E8.MirrorC")])],"isStart":false})});
            var Q3;
            Q3=makeQuery(id+"F6.boolean.opBoolean","COPY",FACE,{"derivedFrom":makeQuery(id+"F6.opExtrude","CAP_FACE",FACE,{"disambiguationData":[OSD([sQuery(id+"F1.wireOp",EDGE,"E9.MirrorC")])],"isStart":false})});
            fillet(context, id + "F8", {"entities" : qUnion([Q0, Q1, Q2, Q3]), "radius" : 3 * mm, "tangentPropagation" : true, "allowEdgeOverflow" : false});
        }
        {
            var Q0;
            Q0=makeQuery(id+"F1.imprint","IMPRINT",FACE,{"disambiguationData":[TD([[makeQuery(id+"F1.imprint","IMPRINT",EDGE,{"derivedFrom":sQuery(id+"F1.wireOp",EDGE,"E6")}),-1.0]])]});
            var sketch = newSketch(context, id + "F9", { "sketchPlane" : qUnion([Q0])});
            skLineSegment(sketch, "E78.bottom", {"start": v(-33.4, 50.05) * mm, "end": v(-35.4, 50.05) * mm});
            skLineSegment(sketch, "E78.top", {"start": v(-33.4, 48.05) * mm, "end": v(-35.4, 48.05) * mm});
            skLineSegment(sketch, "E78.left", {"start": v(-32.9, 49.55) * mm, "end": v(-32.9, 48.55) * mm});
            skLineSegment(sketch, "E78.right", {"start": v(-35.9, 49.55) * mm, "end": v(-35.9, 48.55) * mm});
            skPoint(sketch, "E78.middle", {"position": v(-34.4, 49.05) * mm});
            skPoint(sketch, "E79.visualSharp", {"position": v(-32.9, 50.05) * mm});
            skArc(sketch, "E79.filletArc", {"start": v(-32.9, 49.55) * mm, "mid": v(-33.05, 49.9) * mm, "end": v(-33.4, 50.05) * mm});
            skPoint(sketch, "E80.visualSharp", {"position": v(-32.9, 48.05) * mm});
            skArc(sketch, "E80.filletArc", {"start": v(-33.4, 48.05) * mm, "mid": v(-33.05, 48.2) * mm, "end": v(-32.9, 48.55) * mm});
            skPoint(sketch, "E81.visualSharp", {"position": v(-35.9, 48.05) * mm});
            skArc(sketch, "E81.filletArc", {"start": v(-35.9, 48.55) * mm, "mid": v(-35.75, 48.2) * mm, "end": v(-35.4, 48.05) * mm});
            skPoint(sketch, "E82.visualSharp", {"position": v(-35.9, 50.05) * mm});
            skArc(sketch, "E82.filletArc", {"start": v(-35.4, 50.05) * mm, "mid": v(-35.75, 49.9) * mm, "end": v(-35.9, 49.55) * mm});
            skLineSegment(sketch, "E83.MirrorCS", {"start": v(33.4, 48.05) * mm, "end": v(35.4, 48.05) * mm});
            skLineSegment(sketch, "E84.MirrorCS", {"start": v(35.9, 49.55) * mm, "end": v(35.9, 48.55) * mm});
            skLineSegment(sketch, "E85.MirrorCS", {"start": v(33.4, 50.05) * mm, "end": v(35.4, 50.05) * mm});
            skLineSegment(sketch, "E86.MirrorCS", {"start": v(32.9, 49.55) * mm, "end": v(32.9, 48.55) * mm});
            skArc(sketch, "E87.MirrorCS", {"start": v(32.9, 49.55) * mm, "mid": v(33.05, 49.9) * mm, "end": v(33.4, 50.05) * mm});
            skArc(sketch, "E88.MirrorCS", {"start": v(33.4, 48.05) * mm, "mid": v(33.05, 48.2) * mm, "end": v(32.9, 48.55) * mm});
            skArc(sketch, "E89.MirrorCS", {"start": v(35.9, 48.55) * mm, "mid": v(35.75, 48.2) * mm, "end": v(35.4, 48.05) * mm});
            skArc(sketch, "E90.MirrorCS", {"start": v(35.4, 50.05) * mm, "mid": v(35.75, 49.9) * mm, "end": v(35.9, 49.55) * mm});
            skLineSegment(sketch, "E91.MirrorCS", {"start": v(33.4, -48.05) * mm, "end": v(35.4, -48.05) * mm});
            skLineSegment(sketch, "E92.MirrorCS", {"start": v(33.4, -50.05) * mm, "end": v(35.4, -50.05) * mm});
            skLineSegment(sketch, "E93.MirrorCS", {"start": v(32.9, -49.55) * mm, "end": v(32.9, -48.55) * mm});
            skLineSegment(sketch, "E94.MirrorCS", {"start": v(35.9, -49.55) * mm, "end": v(35.9, -48.55) * mm});
            skArc(sketch, "E95.MirrorCS", {"start": v(35.4, -50.05) * mm, "mid": v(35.75, -49.9) * mm, "end": v(35.9, -49.55) * mm});
            skArc(sketch, "E96.MirrorCS", {"start": v(32.9, -49.55) * mm, "mid": v(33.05, -49.9) * mm, "end": v(33.4, -50.05) * mm});
            skArc(sketch, "E97.MirrorCS", {"start": v(33.4, -48.05) * mm, "mid": v(33.05, -48.2) * mm, "end": v(32.9, -48.55) * mm});
            skArc(sketch, "E98.MirrorCS", {"start": v(35.9, -48.55) * mm, "mid": v(35.75, -48.2) * mm, "end": v(35.4, -48.05) * mm});
            skLineSegment(sketch, "E99.MirrorCS", {"start": v(-33.4, -48.05) * mm, "end": v(-35.4, -48.05) * mm});
            skArc(sketch, "E100.MirrorCS", {"start": v(-35.9, -48.55) * mm, "mid": v(-35.75, -48.2) * mm, "end": v(-35.4, -48.05) * mm});
            skLineSegment(sketch, "E101.MirrorCS", {"start": v(-35.9, -49.55) * mm, "end": v(-35.9, -48.55) * mm});
            skArc(sketch, "E102.MirrorCS", {"start": v(-35.4, -50.05) * mm, "mid": v(-35.75, -49.9) * mm, "end": v(-35.9, -49.55) * mm});
            skLineSegment(sketch, "E103.MirrorCS", {"start": v(-33.4, -50.05) * mm, "end": v(-35.4, -50.05) * mm});
            skArc(sketch, "E104.MirrorCS", {"start": v(-32.9, -49.55) * mm, "mid": v(-33.05, -49.9) * mm, "end": v(-33.4, -50.05) * mm});
            skLineSegment(sketch, "E105.MirrorCS", {"start": v(-32.9, -49.55) * mm, "end": v(-32.9, -48.55) * mm});
            skArc(sketch, "E106.MirrorCS", {"start": v(-33.4, -48.05) * mm, "mid": v(-33.05, -48.2) * mm, "end": v(-32.9, -48.55) * mm});
            skSolve(sketch);
        }
        {
            var Q0;
            Q0 = qSketchRegion(id + "F9", true);
            extrude(context, id + "F10", {"entities" : qUnion([Q0]), "operationType" : NewBodyOperationType.REMOVE, "depth" : 4 * mm});
        }
        {
            var Q0;
            Q0=makeQuery(id+"F2.opExtrude","CAP_EDGE",EDGE,{"disambiguationData":[OSD([sQuery(id+"F1.wireOp",EDGE,"E23.MirrorCS")])],"isStart":true});
            var Q1;
            Q1=makeQuery(id+"F2.opExtrude","CAP_EDGE",EDGE,{"disambiguationData":[OSD([sQuery(id+"F1.wireOp",EDGE,"E22.MirrorCS")])],"isStart":true});
            var Q2;
            Q2=makeQuery(id+"F2.opExtrude","CAP_EDGE",EDGE,{"disambiguationData":[OSD([sQuery(id+"F1.wireOp",EDGE,"E21.MirrorCS")])],"isStart":true});
            var Q3;
            Q3=makeQuery(id+"F2.opExtrude","CAP_EDGE",EDGE,{"disambiguationData":[OSD([sQuery(id+"F1.wireOp",EDGE,"E25.MirrorCS")])],"isStart":true});
            var Q4;
            Q4=makeQuery(id+"F2.opExtrude","CAP_EDGE",EDGE,{"disambiguationData":[OSD([sQuery(id+"F1.wireOp",EDGE,"E24.MirrorCS")])],"isStart":true});
            var Q5;
            Q5=makeQuery(id+"F2.opExtrude","CAP_EDGE",EDGE,{"disambiguationData":[OSD([sQuery(id+"F1.wireOp",EDGE,"E27.MirrorCS")])],"isStart":true});
            var Q6;
            Q6=makeQuery(id+"F2.opExtrude","CAP_EDGE",EDGE,{"disambiguationData":[OSD([sQuery(id+"F1.wireOp",EDGE,"E26.MirrorCS")])],"isStart":true});
            var Q7;
            Q7=makeQuery(id+"F2.opExtrude","CAP_EDGE",EDGE,{"disambiguationData":[OSD([sQuery(id+"F1.wireOp",EDGE,"E30.MirrorCS")])],"isStart":true});
            var Q8;
            Q8=makeQuery(id+"F2.opExtrude","CAP_EDGE",EDGE,{"disambiguationData":[OSD([sQuery(id+"F1.wireOp",EDGE,"E29.MirrorCS")])],"isStart":true});
            var Q9;
            Q9=makeQuery(id+"F2.opExtrude","CAP_EDGE",EDGE,{"disambiguationData":[OSD([sQuery(id+"F1.wireOp",EDGE,"E28.MirrorCS")])],"isStart":true});
            var Q10;
            Q10=makeQuery(id+"F2.opExtrude","CAP_EDGE",EDGE,{"disambiguationData":[OSD([sQuery(id+"F1.wireOp",EDGE,"E24.MirrorCS")])],"isStart":false});
            var Q11;
            Q11=makeQuery(id+"F2.opExtrude","CAP_EDGE",EDGE,{"disambiguationData":[OSD([sQuery(id+"F1.wireOp",EDGE,"E21.MirrorCS")])],"isStart":false});
            var Q12;
            Q12=makeQuery(id+"F2.opExtrude","CAP_EDGE",EDGE,{"disambiguationData":[OSD([sQuery(id+"F1.wireOp",EDGE,"E22.MirrorCS")])],"isStart":false});
            var Q13;
            Q13=makeQuery(id+"F2.opExtrude","CAP_EDGE",EDGE,{"disambiguationData":[OSD([sQuery(id+"F1.wireOp",EDGE,"E23.MirrorCS")])],"isStart":false});
            var Q14;
            Q14=makeQuery(id+"F2.opExtrude","CAP_EDGE",EDGE,{"disambiguationData":[OSD([sQuery(id+"F1.wireOp",EDGE,"E26.MirrorCS")])],"isStart":false});
            var Q15;
            Q15=makeQuery(id+"F2.opExtrude","CAP_EDGE",EDGE,{"disambiguationData":[OSD([sQuery(id+"F1.wireOp",EDGE,"E30.MirrorCS")])],"isStart":false});
            var Q16;
            Q16=makeQuery(id+"F2.opExtrude","CAP_EDGE",EDGE,{"disambiguationData":[OSD([sQuery(id+"F1.wireOp",EDGE,"E29.MirrorCS")])],"isStart":false});
            var Q17;
            Q17=makeQuery(id+"F2.opExtrude","CAP_EDGE",EDGE,{"disambiguationData":[OSD([sQuery(id+"F1.wireOp",EDGE,"E28.MirrorCS")])],"isStart":false});
            var Q18;
            Q18=makeQuery(id+"F2.opExtrude","CAP_EDGE",EDGE,{"disambiguationData":[OSD([sQuery(id+"F1.wireOp",EDGE,"E27.MirrorCS")])],"isStart":false});
            var Q19;
            Q19=makeQuery(id+"F2.opExtrude","CAP_EDGE",EDGE,{"disambiguationData":[OSD([sQuery(id+"F1.wireOp",EDGE,"E25.MirrorCS")])],"isStart":false});
            var Q20;
            Q20=makeQuery(id+"F2.opExtrude","CAP_EDGE",EDGE,{"disambiguationData":[OSD([sQuery(id+"F1.wireOp",EDGE,"E20")])],"isStart":true});
            var Q21;
            Q21=makeQuery(id+"F2.opExtrude","CAP_EDGE",EDGE,{"disambiguationData":[OSD([sQuery(id+"F1.wireOp",EDGE,"E11.MirrorCS")])],"isStart":true});
            var Q22;
            Q22=makeQuery(id+"F2.opExtrude","CAP_EDGE",EDGE,{"disambiguationData":[OSD([sQuery(id+"F1.wireOp",EDGE,"E14")])],"isStart":true});
            var Q23;
            Q23=makeQuery(id+"F2.opExtrude","CAP_EDGE",EDGE,{"disambiguationData":[OSD([sQuery(id+"F1.wireOp",EDGE,"E13")])],"isStart":true});
            var Q24;
            Q24=makeQuery(id+"F2.opExtrude","CAP_EDGE",EDGE,{"disambiguationData":[OSD([sQuery(id+"F1.wireOp",EDGE,"E12.MirrorCS")])],"isStart":true});
            var Q25;
            Q25=makeQuery(id+"F2.opExtrude","CAP_EDGE",EDGE,{"disambiguationData":[OSD([sQuery(id+"F1.wireOp",EDGE,"E19")])],"isStart":true});
            var Q26;
            Q26=makeQuery(id+"F2.opExtrude","CAP_EDGE",EDGE,{"disambiguationData":[OSD([sQuery(id+"F1.wireOp",EDGE,"E15.MirrorCS")])],"isStart":true});
            var Q27;
            Q27=makeQuery(id+"F2.opExtrude","CAP_EDGE",EDGE,{"disambiguationData":[OSD([sQuery(id+"F1.wireOp",EDGE,"E16.MirrorCS")])],"isStart":true});
            var Q28;
            Q28=makeQuery(id+"F2.opExtrude","CAP_EDGE",EDGE,{"disambiguationData":[OSD([sQuery(id+"F1.wireOp",EDGE,"E17.MirrorCS")])],"isStart":true});
            var Q29;
            Q29=makeQuery(id+"F2.opExtrude","CAP_EDGE",EDGE,{"disambiguationData":[OSD([sQuery(id+"F1.wireOp",EDGE,"E18.MirrorCS")])],"isStart":true});
            var Q30;
            Q30=makeQuery(id+"F2.opExtrude","CAP_EDGE",EDGE,{"disambiguationData":[OSD([sQuery(id+"F1.wireOp",EDGE,"E20")])],"isStart":false});
            var Q31;
            Q31=makeQuery(id+"F2.opExtrude","CAP_EDGE",EDGE,{"disambiguationData":[OSD([sQuery(id+"F1.wireOp",EDGE,"E11.MirrorCS")])],"isStart":false});
            var Q32;
            Q32=makeQuery(id+"F2.opExtrude","CAP_EDGE",EDGE,{"disambiguationData":[OSD([sQuery(id+"F1.wireOp",EDGE,"E14")])],"isStart":false});
            var Q33;
            Q33=makeQuery(id+"F2.opExtrude","CAP_EDGE",EDGE,{"disambiguationData":[OSD([sQuery(id+"F1.wireOp",EDGE,"E13")])],"isStart":false});
            var Q34;
            Q34=makeQuery(id+"F2.opExtrude","CAP_EDGE",EDGE,{"disambiguationData":[OSD([sQuery(id+"F1.wireOp",EDGE,"E18.MirrorCS")])],"isStart":false});
            var Q35;
            Q35=makeQuery(id+"F2.opExtrude","CAP_EDGE",EDGE,{"disambiguationData":[OSD([sQuery(id+"F1.wireOp",EDGE,"E17.MirrorCS")])],"isStart":false});
            var Q36;
            Q36=makeQuery(id+"F2.opExtrude","CAP_EDGE",EDGE,{"disambiguationData":[OSD([sQuery(id+"F1.wireOp",EDGE,"E12.MirrorCS")])],"isStart":false});
            var Q37;
            Q37=makeQuery(id+"F2.opExtrude","CAP_EDGE",EDGE,{"disambiguationData":[OSD([sQuery(id+"F1.wireOp",EDGE,"E19")])],"isStart":false});
            var Q38;
            Q38=makeQuery(id+"F2.opExtrude","CAP_EDGE",EDGE,{"disambiguationData":[OSD([sQuery(id+"F1.wireOp",EDGE,"E15.MirrorCS")])],"isStart":false});
            var Q39;
            Q39=makeQuery(id+"F2.opExtrude","CAP_EDGE",EDGE,{"disambiguationData":[OSD([sQuery(id+"F1.wireOp",EDGE,"E16.MirrorCS")])],"isStart":false});
            fillet(context, id + "F11", {"entities" : qUnion([Q0, Q1, Q2, Q3, Q4, Q5, Q6, Q7, Q8, Q9, Q10, Q11, Q12, Q13, Q14, Q15, Q16, Q17, Q18, Q19, Q20, Q21, Q22, Q23, Q24, Q25, Q26, Q27, Q28, Q29, Q30, Q31, Q32, Q33, Q34, Q35, Q36, Q37, Q38, Q39]), "radius" : .5 * mm, "tangentPropagation" : true, "allowEdgeOverflow" : false});
        }
        {
            var Q0;
            Q0=makeQuery(id+"F2.opExtrude","CAP_EDGE",EDGE,{"disambiguationData":[OSD([sQuery(id+"F1.wireOp",EDGE,"E37.left")])],"isStart":false});
            var Q1;
            Q1=makeQuery(id+"F2.opExtrude","CAP_EDGE",EDGE,{"disambiguationData":[OSD([sQuery(id+"F1.wireOp",EDGE,"E37.right")])],"isStart":false});
            var Q2;
            Q2=makeQuery(id+"F2.opExtrude","CAP_EDGE",EDGE,{"disambiguationData":[OSD([sQuery(id+"F1.wireOp",EDGE,"E46.MirrorCS")])],"isStart":false});
            var Q3;
            Q3=makeQuery(id+"F2.opExtrude","CAP_EDGE",EDGE,{"disambiguationData":[OSD([sQuery(id+"F1.wireOp",EDGE,"E47.MirrorCS")])],"isStart":false});
            var Q4;
            Q4=makeQuery(id+"F2.opExtrude","CAP_EDGE",EDGE,{"disambiguationData":[OSD([sQuery(id+"F1.wireOp",EDGE,"E37.left")])],"isStart":true});
            var Q5;
            Q5=makeQuery(id+"F2.opExtrude","CAP_EDGE",EDGE,{"disambiguationData":[OSD([sQuery(id+"F1.wireOp",EDGE,"E37.right")])],"isStart":true});
            var Q6;
            Q6=makeQuery(id+"F2.opExtrude","CAP_EDGE",EDGE,{"disambiguationData":[OSD([sQuery(id+"F1.wireOp",EDGE,"E46.MirrorCS")])],"isStart":true});
            var Q7;
            Q7=makeQuery(id+"F2.opExtrude","CAP_EDGE",EDGE,{"disambiguationData":[OSD([sQuery(id+"F1.wireOp",EDGE,"E47.MirrorCS")])],"isStart":true});
            fillet(context, id + "F12", {"entities" : qUnion([Q0, Q1, Q2, Q3, Q4, Q5, Q6, Q7]), "radius" : .5 * mm, "tangentPropagation" : true, "allowEdgeOverflow" : false});
        }
        {
            var Q0;
            Q0=makeQuery(id+"F2.opExtrude","CAP_EDGE",EDGE,{"disambiguationData":[OSD([sQuery(id+"F1.wireOp",EDGE,"E9.MirrorC")])],"isStart":true});
            var Q1;
            Q1=makeQuery(id+"F2.opExtrude","CAP_EDGE",EDGE,{"disambiguationData":[OSD([sQuery(id+"F1.wireOp",EDGE,"E8.MirrorC")])],"isStart":true});
            var Q2;
            Q2=makeQuery(id+"F2.opExtrude","CAP_EDGE",EDGE,{"disambiguationData":[OSD([sQuery(id+"F1.wireOp",EDGE,"E7.MirrorC")])],"isStart":true});
            var Q3;
            Q3=makeQuery(id+"F2.opExtrude","CAP_EDGE",EDGE,{"disambiguationData":[OSD([sQuery(id+"F1.wireOp",EDGE,"E6")])],"isStart":true});
            fillet(context, id + "F13", {"entities" : qUnion([Q0, Q1, Q2, Q3]), "radius" : .5 * mm, "tangentPropagation" : true, "allowEdgeOverflow" : false});
        }
        {
            var Q0;
            Q0=makeQuery(id+"F2.opExtrude","CAP_EDGE",EDGE,{"disambiguationData":[OSD([sQuery(id+"F1.wireOp",EDGE,"E36")])],"isStart":false});
            var Q1;
            Q1=makeQuery(id+"F2.opExtrude","CAP_EDGE",EDGE,{"disambiguationData":[OSD([sQuery(id+"F1.wireOp",EDGE,"E31")])],"isStart":false});
            var Q2;
            Q2=makeQuery(id+"F2.opExtrude","CAP_EDGE",EDGE,{"disambiguationData":[OSD([sQuery(id+"F1.wireOp",EDGE,"E5")])],"isStart":false});
            var Q3;
            Q3=makeQuery(id+"F2.opExtrude","CAP_EDGE",EDGE,{"disambiguationData":[OSD([sQuery(id+"F1.wireOp",EDGE,"E52.trimOffspring")])],"isStart":false});
            var Q4;
            Q4=makeQuery(id+"F2.opExtrude","CAP_EDGE",EDGE,{"disambiguationData":[OSD([sQuery(id+"F1.wireOp",EDGE,"E56.trimOffspring")])],"isStart":false});
            var Q5;
            Q5=makeQuery(id+"F2.opExtrude","CAP_EDGE",EDGE,{"disambiguationData":[OSD([sQuery(id+"F1.wireOp",EDGE,"E33.MirrorCS")])],"isStart":false});
            var Q6;
            Q6=makeQuery(id+"F2.opExtrude","CAP_EDGE",EDGE,{"disambiguationData":[OSD([sQuery(id+"F1.wireOp",EDGE,"E51")])],"isStart":false});
            var Q7;
            Q7=makeQuery(id+"F2.opExtrude","CAP_EDGE",EDGE,{"disambiguationData":[OSD([sQuery(id+"F1.wireOp",EDGE,"E35.MirrorCS")])],"isStart":false});
            var Q8;
            Q8=makeQuery(id+"F2.opExtrude","CAP_EDGE",EDGE,{"disambiguationData":[OSD([sQuery(id+"F1.wireOp",EDGE,"E34.MirrorCS")])],"isStart":false});
            var Q9;
            Q9=makeQuery(id+"F2.opExtrude","CAP_EDGE",EDGE,{"disambiguationData":[OSD([sQuery(id+"F1.wireOp",EDGE,"E58.trimOffspring")])],"isStart":false});
            var Q10;
            Q10=makeQuery(id+"F2.opExtrude","CAP_EDGE",EDGE,{"disambiguationData":[OSD([sQuery(id+"F1.wireOp",EDGE,"E57.trimOffspring")])],"isStart":false});
            var Q11;
            Q11=makeQuery(id+"F2.opExtrude","CAP_EDGE",EDGE,{"disambiguationData":[OSD([sQuery(id+"F1.wireOp",EDGE,"E32.MirrorCS")])],"isStart":false});
            var Q12;
            Q12=makeQuery(id+"F2.opExtrude","CAP_EDGE",EDGE,{"disambiguationData":[OSD([sQuery(id+"F1.wireOp",EDGE,"E35.MirrorCS")])],"isStart":true});
            var Q13;
            Q13=makeQuery(id+"F2.opExtrude","CAP_EDGE",EDGE,{"disambiguationData":[OSD([sQuery(id+"F1.wireOp",EDGE,"E32.MirrorCS")])],"isStart":true});
            var Q14;
            Q14=makeQuery(id+"F2.opExtrude","CAP_EDGE",EDGE,{"disambiguationData":[OSD([sQuery(id+"F1.wireOp",EDGE,"E57.trimOffspring")])],"isStart":true});
            var Q15;
            Q15=makeQuery(id+"F2.opExtrude","CAP_EDGE",EDGE,{"disambiguationData":[OSD([sQuery(id+"F1.wireOp",EDGE,"E58.trimOffspring")])],"isStart":true});
            var Q16;
            Q16=makeQuery(id+"F2.opExtrude","CAP_EDGE",EDGE,{"disambiguationData":[OSD([sQuery(id+"F1.wireOp",EDGE,"E3.MirrorC")])],"isStart":true});
            var Q17;
            Q17=makeQuery(id+"F2.opExtrude","CAP_EDGE",EDGE,{"disambiguationData":[OSD([sQuery(id+"F1.wireOp",EDGE,"E34.MirrorCS")])],"isStart":true});
            var Q18;
            Q18=makeQuery(id+"F2.opExtrude","CAP_EDGE",EDGE,{"disambiguationData":[OSD([sQuery(id+"F1.wireOp",EDGE,"E4.MirrorC")])],"isStart":true});
            var Q19;
            {var subQ0=sQuery(id+"F1.wireOp",EDGE,"E37.left");Q19=makeQuery(id+"F12.opFillet","BLEND_EDGE",EDGE,{"blendedFrom":[makeQuery(id+"F2.opExtrude","CAP_EDGE",EDGE,{"disambiguationData":[OSD([subQ0])],"isStart":true}),makeQuery(id+"F2.opExtrude","CAP_FACE",FACE,{"disambiguationData":[OSD([sQuery(id+"F1.wireOp",EDGE,"E1"),sQuery(id+"F1.wireOp",EDGE,"E2.MirrorC"),sQuery(id+"F1.wireOp",EDGE,"E3.MirrorC"),sQuery(id+"F1.wireOp",EDGE,"E4.MirrorC"),sQuery(id+"F1.wireOp",EDGE,"E5"),sQuery(id+"F1.wireOp",EDGE,"E6"),sQuery(id+"F1.wireOp",EDGE,"E7.MirrorC"),sQuery(id+"F1.wireOp",EDGE,"E8.MirrorC"),sQuery(id+"F1.wireOp",EDGE,"E9.MirrorC"),sQuery(id+"F1.wireOp",EDGE,"E11.MirrorCS"),sQuery(id+"F1.wireOp",EDGE,"E12.MirrorCS"),sQuery(id+"F1.wireOp",EDGE,"E13"),sQuery(id+"F1.wireOp",EDGE,"E14"),sQuery(id+"F1.wireOp",EDGE,"E15.MirrorCS"),sQuery(id+"F1.wireOp",EDGE,"E16.MirrorCS"),sQuery(id+"F1.wireOp",EDGE,"E17.MirrorCS"),sQuery(id+"F1.wireOp",EDGE,"E18.MirrorCS"),sQuery(id+"F1.wireOp",EDGE,"E19"),sQuery(id+"F1.wireOp",EDGE,"E20"),sQuery(id+"F1.wireOp",EDGE,"E21.MirrorCS"),sQuery(id+"F1.wireOp",EDGE,"E22.MirrorCS"),sQuery(id+"F1.wireOp",EDGE,"E23.MirrorCS"),sQuery(id+"F1.wireOp",EDGE,"E24.MirrorCS"),sQuery(id+"F1.wireOp",EDGE,"E25.MirrorCS"),sQuery(id+"F1.wireOp",EDGE,"E26.MirrorCS"),sQuery(id+"F1.wireOp",EDGE,"E27.MirrorCS"),sQuery(id+"F1.wireOp",EDGE,"E28.MirrorCS"),sQuery(id+"F1.wireOp",EDGE,"E29.MirrorCS"),sQuery(id+"F1.wireOp",EDGE,"E30.MirrorCS"),sQuery(id+"F1.wireOp",EDGE,"E31"),sQuery(id+"F1.wireOp",EDGE,"E32.MirrorCS"),sQuery(id+"F1.wireOp",EDGE,"E33.MirrorCS"),sQuery(id+"F1.wireOp",EDGE,"E34.MirrorCS"),sQuery(id+"F1.wireOp",EDGE,"E35.MirrorCS"),sQuery(id+"F1.wireOp",EDGE,"E36"),sQuery(id+"F1.wireOp",EDGE,"E37.bottom"),sQuery(id+"F1.wireOp",EDGE,"E37.top"),subQ0,sQuery(id+"F1.wireOp",EDGE,"E37.right"),sQuery(id+"F1.wireOp",EDGE,"E39.filletArc"),sQuery(id+"F1.wireOp",EDGE,"E40.filletArc"),sQuery(id+"F1.wireOp",EDGE,"E41.filletArc"),sQuery(id+"F1.wireOp",EDGE,"E42.filletArc"),sQuery(id+"F1.wireOp",EDGE,"E43.MirrorCS"),sQuery(id+"F1.wireOp",EDGE,"E44.MirrorCS"),sQuery(id+"F1.wireOp",EDGE,"E45.MirrorCS"),sQuery(id+"F1.wireOp",EDGE,"E46.MirrorCS"),sQuery(id+"F1.wireOp",EDGE,"E47.MirrorCS"),sQuery(id+"F1.wireOp",EDGE,"E48.MirrorCS"),sQuery(id+"F1.wireOp",EDGE,"E49.MirrorCS"),sQuery(id+"F1.wireOp",EDGE,"E50.MirrorCS"),sQuery(id+"F1.wireOp",EDGE,"E51"),sQuery(id+"F1.wireOp",EDGE,"E52.trimOffspring"),sQuery(id+"F1.wireOp",EDGE,"E53"),sQuery(id+"F1.wireOp",EDGE,"b30a117b-d75a-4502-b387-7b125c7515d1.trimOffspring"),sQuery(id+"F1.wireOp",EDGE,"E54"),sQuery(id+"F1.wireOp",EDGE,"E55.MirrorCS"),sQuery(id+"F1.wireOp",EDGE,"E56.trimOffspring"),sQuery(id+"F1.wireOp",EDGE,"E57.trimOffspring"),sQuery(id+"F1.wireOp",EDGE,"E58.trimOffspring"),sQuery(id+"F1.wireOp",EDGE,"XfeBEER9-2g1J-kN3v-mQVF-R0Wur47D0a7y"),sQuery(id+"F1.wireOp",EDGE,"cj9tdcR5-JuoR-tGsP-MGoO-S5KOOCOVeEPM"),sQuery(id+"F1.wireOp",EDGE,"E59.MirrorCS"),sQuery(id+"F1.wireOp",EDGE,"E60.MirrorCS"),sQuery(id+"F1.wireOp",EDGE,"c64e98b8-e32c-4987-8556-cb4b40954b380.MirrorCS"),sQuery(id+"F1.wireOp",EDGE,"E61.MirrorCS"),sQuery(id+"F1.wireOp",EDGE,"E62.MirrorCS"),sQuery(id+"F1.wireOp",EDGE,"E63.MirrorCS"),sQuery(id+"F1.wireOp",EDGE,"E64.MirrorCS"),sQuery(id+"F1.wireOp",EDGE,"bcf6c320-8a54-4c53-9ffd-94a113f5b3590.MirrorCS"),sQuery(id+"F1.wireOp",EDGE,"c17ce9da-a2d4-493a-92bd-da0e6258ab510.MirrorCS"),sQuery(id+"F1.wireOp",EDGE,"E65.MirrorCS"),sQuery(id+"F1.wireOp",EDGE,"E66.MirrorCS"),sQuery(id+"F1.wireOp",EDGE,"E67.MirrorCS"),sQuery(id+"F1.wireOp",EDGE,"eab108b2-96d9-45b4-925c-b77b0fad8b6b0.MirrorCS"),sQuery(id+"F1.wireOp",EDGE,"861f5b8e-cbd1-41e1-b2bb-9c07049055a20.MirrorCS")])],"isStart":true})],"blendedInto":[makeQuery(id+"F2.opExtrude","CAP_FACE",FACE,{"disambiguationData":[OSD([sQuery(id+"F1.wireOp",EDGE,"E1"),sQuery(id+"F1.wireOp",EDGE,"E2.MirrorC"),sQuery(id+"F1.wireOp",EDGE,"E3.MirrorC"),sQuery(id+"F1.wireOp",EDGE,"E4.MirrorC"),sQuery(id+"F1.wireOp",EDGE,"E5"),sQuery(id+"F1.wireOp",EDGE,"E6"),sQuery(id+"F1.wireOp",EDGE,"E7.MirrorC"),sQuery(id+"F1.wireOp",EDGE,"E8.MirrorC"),sQuery(id+"F1.wireOp",EDGE,"E9.MirrorC"),sQuery(id+"F1.wireOp",EDGE,"E11.MirrorCS"),sQuery(id+"F1.wireOp",EDGE,"E12.MirrorCS"),sQuery(id+"F1.wireOp",EDGE,"E13"),sQuery(id+"F1.wireOp",EDGE,"E14"),sQuery(id+"F1.wireOp",EDGE,"E15.MirrorCS"),sQuery(id+"F1.wireOp",EDGE,"E16.MirrorCS"),sQuery(id+"F1.wireOp",EDGE,"E17.MirrorCS"),sQuery(id+"F1.wireOp",EDGE,"E18.MirrorCS"),sQuery(id+"F1.wireOp",EDGE,"E19"),sQuery(id+"F1.wireOp",EDGE,"E20"),sQuery(id+"F1.wireOp",EDGE,"E21.MirrorCS"),sQuery(id+"F1.wireOp",EDGE,"E22.MirrorCS"),sQuery(id+"F1.wireOp",EDGE,"E23.MirrorCS"),sQuery(id+"F1.wireOp",EDGE,"E24.MirrorCS"),sQuery(id+"F1.wireOp",EDGE,"E25.MirrorCS"),sQuery(id+"F1.wireOp",EDGE,"E26.MirrorCS"),sQuery(id+"F1.wireOp",EDGE,"E27.MirrorCS"),sQuery(id+"F1.wireOp",EDGE,"E28.MirrorCS"),sQuery(id+"F1.wireOp",EDGE,"E29.MirrorCS"),sQuery(id+"F1.wireOp",EDGE,"E30.MirrorCS"),sQuery(id+"F1.wireOp",EDGE,"E31"),sQuery(id+"F1.wireOp",EDGE,"E32.MirrorCS"),sQuery(id+"F1.wireOp",EDGE,"E33.MirrorCS"),sQuery(id+"F1.wireOp",EDGE,"E34.MirrorCS"),sQuery(id+"F1.wireOp",EDGE,"E35.MirrorCS"),sQuery(id+"F1.wireOp",EDGE,"E36"),sQuery(id+"F1.wireOp",EDGE,"E37.bottom"),sQuery(id+"F1.wireOp",EDGE,"E37.top"),subQ0,sQuery(id+"F1.wireOp",EDGE,"E37.right"),sQuery(id+"F1.wireOp",EDGE,"E39.filletArc"),sQuery(id+"F1.wireOp",EDGE,"E40.filletArc"),sQuery(id+"F1.wireOp",EDGE,"E41.filletArc"),sQuery(id+"F1.wireOp",EDGE,"E42.filletArc"),sQuery(id+"F1.wireOp",EDGE,"E43.MirrorCS"),sQuery(id+"F1.wireOp",EDGE,"E44.MirrorCS"),sQuery(id+"F1.wireOp",EDGE,"E45.MirrorCS"),sQuery(id+"F1.wireOp",EDGE,"E46.MirrorCS"),sQuery(id+"F1.wireOp",EDGE,"E47.MirrorCS"),sQuery(id+"F1.wireOp",EDGE,"E48.MirrorCS"),sQuery(id+"F1.wireOp",EDGE,"E49.MirrorCS"),sQuery(id+"F1.wireOp",EDGE,"E50.MirrorCS"),sQuery(id+"F1.wireOp",EDGE,"E51"),sQuery(id+"F1.wireOp",EDGE,"E52.trimOffspring"),sQuery(id+"F1.wireOp",EDGE,"E53"),sQuery(id+"F1.wireOp",EDGE,"b30a117b-d75a-4502-b387-7b125c7515d1.trimOffspring"),sQuery(id+"F1.wireOp",EDGE,"E54"),sQuery(id+"F1.wireOp",EDGE,"E55.MirrorCS"),sQuery(id+"F1.wireOp",EDGE,"E56.trimOffspring"),sQuery(id+"F1.wireOp",EDGE,"E57.trimOffspring"),sQuery(id+"F1.wireOp",EDGE,"E58.trimOffspring"),sQuery(id+"F1.wireOp",EDGE,"XfeBEER9-2g1J-kN3v-mQVF-R0Wur47D0a7y"),sQuery(id+"F1.wireOp",EDGE,"cj9tdcR5-JuoR-tGsP-MGoO-S5KOOCOVeEPM"),sQuery(id+"F1.wireOp",EDGE,"E59.MirrorCS"),sQuery(id+"F1.wireOp",EDGE,"E60.MirrorCS"),sQuery(id+"F1.wireOp",EDGE,"c64e98b8-e32c-4987-8556-cb4b40954b380.MirrorCS"),sQuery(id+"F1.wireOp",EDGE,"E61.MirrorCS"),sQuery(id+"F1.wireOp",EDGE,"E62.MirrorCS"),sQuery(id+"F1.wireOp",EDGE,"E63.MirrorCS"),sQuery(id+"F1.wireOp",EDGE,"E64.MirrorCS"),sQuery(id+"F1.wireOp",EDGE,"bcf6c320-8a54-4c53-9ffd-94a113f5b3590.MirrorCS"),sQuery(id+"F1.wireOp",EDGE,"c17ce9da-a2d4-493a-92bd-da0e6258ab510.MirrorCS"),sQuery(id+"F1.wireOp",EDGE,"E65.MirrorCS"),sQuery(id+"F1.wireOp",EDGE,"E66.MirrorCS"),sQuery(id+"F1.wireOp",EDGE,"E67.MirrorCS"),sQuery(id+"F1.wireOp",EDGE,"eab108b2-96d9-45b4-925c-b77b0fad8b6b0.MirrorCS"),sQuery(id+"F1.wireOp",EDGE,"861f5b8e-cbd1-41e1-b2bb-9c07049055a20.MirrorCS")])],"isStart":true})]});}
            var Q20;
            Q20=makeQuery(id+"F2.opExtrude","CAP_EDGE",EDGE,{"disambiguationData":[OSD([sQuery(id+"F1.wireOp",EDGE,"E51")])],"isStart":true});
            var Q21;
            Q21=makeQuery(id+"F2.opExtrude","CAP_EDGE",EDGE,{"disambiguationData":[OSD([sQuery(id+"F1.wireOp",EDGE,"E36")])],"isStart":true});
            var Q22;
            Q22=makeQuery(id+"F2.opExtrude","CAP_EDGE",EDGE,{"disambiguationData":[OSD([sQuery(id+"F1.wireOp",EDGE,"E33.MirrorCS")])],"isStart":true});
            var Q23;
            Q23=makeQuery(id+"F2.opExtrude","CAP_EDGE",EDGE,{"disambiguationData":[OSD([sQuery(id+"F1.wireOp",EDGE,"E31")])],"isStart":true});
            var Q24;
            Q24=makeQuery(id+"F2.opExtrude","CAP_EDGE",EDGE,{"disambiguationData":[OSD([sQuery(id+"F1.wireOp",EDGE,"E1")])],"isStart":true});
            var Q25;
            Q25=makeQuery(id+"F2.opExtrude","CAP_EDGE",EDGE,{"disambiguationData":[OSD([sQuery(id+"F1.wireOp",EDGE,"E5")])],"isStart":true});
            var Q26;
            Q26=makeQuery(id+"F2.opExtrude","CAP_EDGE",EDGE,{"disambiguationData":[OSD([sQuery(id+"F1.wireOp",EDGE,"E52.trimOffspring")])],"isStart":true});
            var Q27;
            Q27=makeQuery(id+"F2.opExtrude","CAP_EDGE",EDGE,{"disambiguationData":[OSD([sQuery(id+"F1.wireOp",EDGE,"E56.trimOffspring")])],"isStart":true});
            var Q28;
            Q28=makeQuery(id+"F2.opExtrude","CAP_EDGE",EDGE,{"disambiguationData":[OSD([sQuery(id+"F1.wireOp",EDGE,"E2.MirrorC")])],"isStart":true});
            fillet(context, id + "F14", {"entities" : qUnion([Q0, Q1, Q2, Q3, Q4, Q5, Q6, Q7, Q8, Q9, Q10, Q11, Q12, Q13, Q14, Q15, Q16, Q17, Q18, Q19, Q20, Q21, Q22, Q23, Q24, Q25, Q26, Q27, Q28]), "radius" : .5 * mm, "tangentPropagation" : true, "allowEdgeOverflow" : false});
        }
        {
            var Q0;
            Q0=makeQuery(id+"F2.opExtrude","CAP_FACE",FACE,{"disambiguationData":[OSD([sQuery(id+"F1.wireOp",EDGE,"E1"),sQuery(id+"F1.wireOp",EDGE,"E2.MirrorC"),sQuery(id+"F1.wireOp",EDGE,"E3.MirrorC"),sQuery(id+"F1.wireOp",EDGE,"E4.MirrorC"),sQuery(id+"F1.wireOp",EDGE,"E5"),sQuery(id+"F1.wireOp",EDGE,"E6"),sQuery(id+"F1.wireOp",EDGE,"E7.MirrorC"),sQuery(id+"F1.wireOp",EDGE,"E8.MirrorC"),sQuery(id+"F1.wireOp",EDGE,"E9.MirrorC"),sQuery(id+"F1.wireOp",EDGE,"E11.MirrorCS"),sQuery(id+"F1.wireOp",EDGE,"E12.MirrorCS"),sQuery(id+"F1.wireOp",EDGE,"E13"),sQuery(id+"F1.wireOp",EDGE,"E14"),sQuery(id+"F1.wireOp",EDGE,"E15.MirrorCS"),sQuery(id+"F1.wireOp",EDGE,"E16.MirrorCS"),sQuery(id+"F1.wireOp",EDGE,"E17.MirrorCS"),sQuery(id+"F1.wireOp",EDGE,"E18.MirrorCS"),sQuery(id+"F1.wireOp",EDGE,"E19"),sQuery(id+"F1.wireOp",EDGE,"E20"),sQuery(id+"F1.wireOp",EDGE,"E21.MirrorCS"),sQuery(id+"F1.wireOp",EDGE,"E22.MirrorCS"),sQuery(id+"F1.wireOp",EDGE,"E23.MirrorCS"),sQuery(id+"F1.wireOp",EDGE,"E24.MirrorCS"),sQuery(id+"F1.wireOp",EDGE,"E25.MirrorCS"),sQuery(id+"F1.wireOp",EDGE,"E26.MirrorCS"),sQuery(id+"F1.wireOp",EDGE,"E27.MirrorCS"),sQuery(id+"F1.wireOp",EDGE,"E28.MirrorCS"),sQuery(id+"F1.wireOp",EDGE,"E29.MirrorCS"),sQuery(id+"F1.wireOp",EDGE,"E30.MirrorCS"),sQuery(id+"F1.wireOp",EDGE,"E31"),sQuery(id+"F1.wireOp",EDGE,"E32.MirrorCS"),sQuery(id+"F1.wireOp",EDGE,"E33.MirrorCS"),sQuery(id+"F1.wireOp",EDGE,"E34.MirrorCS"),sQuery(id+"F1.wireOp",EDGE,"E35.MirrorCS"),sQuery(id+"F1.wireOp",EDGE,"E36"),sQuery(id+"F1.wireOp",EDGE,"E37.bottom"),sQuery(id+"F1.wireOp",EDGE,"E37.top"),sQuery(id+"F1.wireOp",EDGE,"E37.left"),sQuery(id+"F1.wireOp",EDGE,"E37.right"),sQuery(id+"F1.wireOp",EDGE,"E39.filletArc"),sQuery(id+"F1.wireOp",EDGE,"E40.filletArc"),sQuery(id+"F1.wireOp",EDGE,"E41.filletArc"),sQuery(id+"F1.wireOp",EDGE,"E42.filletArc"),sQuery(id+"F1.wireOp",EDGE,"E43.MirrorCS"),sQuery(id+"F1.wireOp",EDGE,"E44.MirrorCS"),sQuery(id+"F1.wireOp",EDGE,"E45.MirrorCS"),sQuery(id+"F1.wireOp",EDGE,"E46.MirrorCS"),sQuery(id+"F1.wireOp",EDGE,"E47.MirrorCS"),sQuery(id+"F1.wireOp",EDGE,"E48.MirrorCS"),sQuery(id+"F1.wireOp",EDGE,"E49.MirrorCS"),sQuery(id+"F1.wireOp",EDGE,"E50.MirrorCS"),sQuery(id+"F1.wireOp",EDGE,"E51"),sQuery(id+"F1.wireOp",EDGE,"E52.trimOffspring"),sQuery(id+"F1.wireOp",EDGE,"E53"),sQuery(id+"F1.wireOp",EDGE,"b30a117b-d75a-4502-b387-7b125c7515d1.trimOffspring"),sQuery(id+"F1.wireOp",EDGE,"E54"),sQuery(id+"F1.wireOp",EDGE,"E55.MirrorCS"),sQuery(id+"F1.wireOp",EDGE,"E56.trimOffspring"),sQuery(id+"F1.wireOp",EDGE,"E57.trimOffspring"),sQuery(id+"F1.wireOp",EDGE,"E58.trimOffspring"),sQuery(id+"F1.wireOp",EDGE,"XfeBEER9-2g1J-kN3v-mQVF-R0Wur47D0a7y"),sQuery(id+"F1.wireOp",EDGE,"cj9tdcR5-JuoR-tGsP-MGoO-S5KOOCOVeEPM"),sQuery(id+"F1.wireOp",EDGE,"E59.MirrorCS"),sQuery(id+"F1.wireOp",EDGE,"E60.MirrorCS"),sQuery(id+"F1.wireOp",EDGE,"c64e98b8-e32c-4987-8556-cb4b40954b380.MirrorCS"),sQuery(id+"F1.wireOp",EDGE,"E61.MirrorCS"),sQuery(id+"F1.wireOp",EDGE,"E62.MirrorCS"),sQuery(id+"F1.wireOp",EDGE,"E63.MirrorCS"),sQuery(id+"F1.wireOp",EDGE,"E64.MirrorCS"),sQuery(id+"F1.wireOp",EDGE,"bcf6c320-8a54-4c53-9ffd-94a113f5b3590.MirrorCS"),sQuery(id+"F1.wireOp",EDGE,"c17ce9da-a2d4-493a-92bd-da0e6258ab510.MirrorCS"),sQuery(id+"F1.wireOp",EDGE,"E65.MirrorCS"),sQuery(id+"F1.wireOp",EDGE,"E66.MirrorCS"),sQuery(id+"F1.wireOp",EDGE,"E67.MirrorCS"),sQuery(id+"F1.wireOp",EDGE,"eab108b2-96d9-45b4-925c-b77b0fad8b6b0.MirrorCS"),sQuery(id+"F1.wireOp",EDGE,"861f5b8e-cbd1-41e1-b2bb-9c07049055a20.MirrorCS")])],"isStart":false});
            var sketch = newSketch(context, id + "F15", { "sketchPlane" : qUnion([Q0])});
            skPoint(sketch, "E107", {"position": v(17.08, -38.68) * mm});
            skPoint(sketch, "E108", {"position": v(19.36, -40.8) * mm});
            skArc(sketch, "E109", {"start": v(17.08, -38.68) * mm, "mid": v(18.16, -39.8) * mm, "end": v(19.36, -40.8) * mm});
            skPoint(sketch, "E110", {"position": v(17.34, -42.89) * mm});
            skPoint(sketch, "E111", {"position": v(15.3, -41.07) * mm});
            skArc(sketch, "E112", {"start": v(17.34, -42.89) * mm, "mid": v(16.68, -41.58) * mm, "end": v(15.3, -41.07) * mm});
            skPoint(sketch, "E113.right.end.orphan", {"position": v(13.51, -37.55) * mm});
            skArc(sketch, "E114", {"start": v(17.08, -38.68) * mm, "mid": v(14.83, -38.87) * mm, "end": v(15.3, -41.07) * mm});
            skArc(sketch, "E115", {"start": v(17.34, -42.89) * mm, "mid": v(19.54, -43.3) * mm, "end": v(19.71, -41.08) * mm});
            skPoint(sketch, "E116", {"position": v(19.71, -41.08) * mm});
            skLineSegment(sketch, "E117", {"start": v(19.71, -41.08) * mm, "end": v(19.36, -40.8) * mm});
            skArc(sketch, "E118.MirrorCS", {"start": v(-17.08, -38.68) * mm, "mid": v(-14.83, -38.87) * mm, "end": v(-15.3, -41.07) * mm});
            skArc(sketch, "E119.MirrorCS", {"start": v(-17.08, -38.68) * mm, "mid": v(-18.16, -39.8) * mm, "end": v(-19.36, -40.8) * mm});
            skLineSegment(sketch, "E120.MirrorCS", {"start": v(-19.71, -41.08) * mm, "end": v(-19.36, -40.8) * mm});
            skArc(sketch, "E121.MirrorCS", {"start": v(-17.34, -42.89) * mm, "mid": v(-19.54, -43.3) * mm, "end": v(-19.71, -41.08) * mm});
            skArc(sketch, "E122.MirrorCS", {"start": v(-17.34, -42.89) * mm, "mid": v(-16.68, -41.58) * mm, "end": v(-15.3, -41.07) * mm});
            skArc(sketch, "E123.MirrorCS", {"start": v(-17.08, 38.68) * mm, "mid": v(-14.83, 38.87) * mm, "end": v(-15.3, 41.07) * mm});
            skArc(sketch, "E124.MirrorCS", {"start": v(-17.34, 42.89) * mm, "mid": v(-16.68, 41.58) * mm, "end": v(-15.3, 41.07) * mm});
            skArc(sketch, "E125.MirrorCS", {"start": v(-17.34, 42.89) * mm, "mid": v(-19.54, 43.3) * mm, "end": v(-19.71, 41.08) * mm});
            skArc(sketch, "E126.MirrorCS", {"start": v(-17.08, 38.68) * mm, "mid": v(-18.16, 39.8) * mm, "end": v(-19.36, 40.8) * mm});
            skLineSegment(sketch, "E127.MirrorCS", {"start": v(-19.71, 41.08) * mm, "end": v(-19.36, 40.8) * mm});
            skArc(sketch, "E128.MirrorCS", {"start": v(17.08, 38.68) * mm, "mid": v(18.16, 39.8) * mm, "end": v(19.36, 40.8) * mm});
            skArc(sketch, "E129.MirrorCS", {"start": v(17.08, 38.68) * mm, "mid": v(14.83, 38.87) * mm, "end": v(15.3, 41.07) * mm});
            skArc(sketch, "E130.MirrorCS", {"start": v(17.34, 42.89) * mm, "mid": v(16.68, 41.58) * mm, "end": v(15.3, 41.07) * mm});
            skArc(sketch, "E131.MirrorCS", {"start": v(17.34, 42.89) * mm, "mid": v(19.54, 43.3) * mm, "end": v(19.71, 41.08) * mm});
            skLineSegment(sketch, "E132.MirrorCS", {"start": v(19.71, 41.08) * mm, "end": v(19.36, 40.8) * mm});
            skLineSegment(sketch, "E133", {"start": v(16.68, -41.58) * mm, "end": v(18.16, -39.8) * mm, "construction": true});
            skSolve(sketch);
        }
        {
            var Q0;
            Q0 = qSketchRegion(id + "F15", true);
            extrude(context, id + "F16", {"entities" : qUnion([Q0]), "operationType" : NewBodyOperationType.ADD, "depth" : 1 * mm});
        }
        {
            var Q0;
            Q0=makeQuery(id+"F16.opExtrude","CAP_EDGE",EDGE,{"disambiguationData":[OSD([sQuery(id+"F15.wireOp",EDGE,"E112")])],"isStart":false});
            var Q1;
            Q1=makeQuery(id+"F16.opExtrude","CAP_EDGE",EDGE,{"disambiguationData":[OSD([sQuery(id+"F15.wireOp",EDGE,"E114")])],"isStart":false});
            var Q2;
            Q2=makeQuery(id+"F16.opExtrude","CAP_EDGE",EDGE,{"disambiguationData":[OSD([sQuery(id+"F15.wireOp",EDGE,"E109")])],"isStart":false});
            var Q3;
            Q3=makeQuery(id+"F16.opExtrude","CAP_EDGE",EDGE,{"disambiguationData":[OSD([sQuery(id+"F15.wireOp",EDGE,"E115")])],"isStart":false});
            var Q4;
            Q4=makeQuery(id+"F16.opExtrude","CAP_EDGE",EDGE,{"disambiguationData":[OSD([sQuery(id+"F15.wireOp",EDGE,"E117")])],"isStart":false});
            var Q5;
            Q5=makeQuery(id+"F16.opExtrude","CAP_EDGE",EDGE,{"disambiguationData":[OSD([sQuery(id+"F15.wireOp",EDGE,"E121.MirrorCS")])],"isStart":false});
            var Q6;
            Q6=makeQuery(id+"F16.opExtrude","CAP_EDGE",EDGE,{"disambiguationData":[OSD([sQuery(id+"F15.wireOp",EDGE,"E122.MirrorCS")])],"isStart":false});
            var Q7;
            Q7=makeQuery(id+"F16.opExtrude","CAP_EDGE",EDGE,{"disambiguationData":[OSD([sQuery(id+"F15.wireOp",EDGE,"E118.MirrorCS")])],"isStart":false});
            var Q8;
            Q8=makeQuery(id+"F16.opExtrude","CAP_EDGE",EDGE,{"disambiguationData":[OSD([sQuery(id+"F15.wireOp",EDGE,"E119.MirrorCS")])],"isStart":false});
            var Q9;
            Q9=makeQuery(id+"F16.opExtrude","CAP_EDGE",EDGE,{"disambiguationData":[OSD([sQuery(id+"F15.wireOp",EDGE,"E120.MirrorCS")])],"isStart":false});
            var Q10;
            Q10=makeQuery(id+"F16.opExtrude","CAP_EDGE",EDGE,{"disambiguationData":[OSD([sQuery(id+"F15.wireOp",EDGE,"E126.MirrorCS")])],"isStart":false});
            var Q11;
            Q11=makeQuery(id+"F16.opExtrude","CAP_EDGE",EDGE,{"disambiguationData":[OSD([sQuery(id+"F15.wireOp",EDGE,"E127.MirrorCS")])],"isStart":false});
            var Q12;
            Q12=makeQuery(id+"F16.opExtrude","CAP_EDGE",EDGE,{"disambiguationData":[OSD([sQuery(id+"F15.wireOp",EDGE,"E125.MirrorCS")])],"isStart":false});
            var Q13;
            Q13=makeQuery(id+"F16.opExtrude","CAP_EDGE",EDGE,{"disambiguationData":[OSD([sQuery(id+"F15.wireOp",EDGE,"E124.MirrorCS")])],"isStart":false});
            var Q14;
            Q14=makeQuery(id+"F16.opExtrude","CAP_EDGE",EDGE,{"disambiguationData":[OSD([sQuery(id+"F15.wireOp",EDGE,"E123.MirrorCS")])],"isStart":false});
            var Q15;
            Q15=makeQuery(id+"F16.opExtrude","CAP_EDGE",EDGE,{"disambiguationData":[OSD([sQuery(id+"F15.wireOp",EDGE,"E128.MirrorCS")])],"isStart":false});
            var Q16;
            Q16=makeQuery(id+"F16.opExtrude","CAP_EDGE",EDGE,{"disambiguationData":[OSD([sQuery(id+"F15.wireOp",EDGE,"E132.MirrorCS")])],"isStart":false});
            var Q17;
            Q17=makeQuery(id+"F16.opExtrude","CAP_EDGE",EDGE,{"disambiguationData":[OSD([sQuery(id+"F15.wireOp",EDGE,"E131.MirrorCS")])],"isStart":false});
            var Q18;
            Q18=makeQuery(id+"F16.opExtrude","CAP_EDGE",EDGE,{"disambiguationData":[OSD([sQuery(id+"F15.wireOp",EDGE,"E130.MirrorCS")])],"isStart":false});
            var Q19;
            Q19=makeQuery(id+"F16.opExtrude","CAP_EDGE",EDGE,{"disambiguationData":[OSD([sQuery(id+"F15.wireOp",EDGE,"E129.MirrorCS")])],"isStart":false});
            fillet(context, id + "F17", {"entities" : qUnion([Q0, Q1, Q2, Q3, Q4, Q5, Q6, Q7, Q8, Q9, Q10, Q11, Q12, Q13, Q14, Q15, Q16, Q17, Q18, Q19]), "radius" : 1 * mm, "tangentPropagation" : true, "allowEdgeOverflow" : false});
        }
    });
